FCSTD DOCUMENT  (FreeCAD 1.0R39109 (Git))
Label: 16_incher
License: All rights reserved
LicenseURL: http://en.wikipedia.org/wiki/All_rights_reserved
objects: Sketcher::SketchObject×32, Part::Feature×26, App::Part×21, Part::Extrusion×19, Part::FeaturePython×12, PartDesign::Pocket×7, Part::Mirroring×5, PartDesign::Body×4, PartDesign::PolarPattern×3, Part::Fillet×3, PartDesign::Pad×2, Part::Revolution×2, PartDesign::FeatureBase×2, PartDesign::Hole×2, Part::Sphere×1, Part::Cut×1
note: 171 computed .brp shape members not serialized (recipe doc carries the construction recipe); baked Part::Feature solids carry a one-line shape summary decoded from their .brp

FEATURE [Sketcher::SketchObject] Sketch003  label="mirror"
  ArcFitTolerance = 0
  FullyConstrained = false
  MakeInternals = false
  expr: Constraints[6] = 400 * 0.813985
  sketch-geometry (4):
    g0: Circle CenterX=0 CenterY=0 CenterZ=0 NormalX=0 NormalY=0 NormalZ=1 AngleXU=0 Radius=200
    g1: Circle [constr] CenterX=0 CenterY=0 CenterZ=0 NormalX=0 NormalY=0 NormalZ=1 AngleXU=0 Radius=112
    g2: Circle [constr] CenterX=0 CenterY=0 CenterZ=0 NormalX=0 NormalY=0 NormalZ=1 AngleXU=0 Radius=80.1102
    g3: Circle [constr] CenterX=0 CenterY=0 CenterZ=0 NormalX=0 NormalY=0 NormalZ=1 AngleXU=0 Radius=162.797
  constraints (7):
    c: Coincident(g0,g-1)
    c: Diameter(g0) = 400
    c: Coincident(g1,g0)
    c: Radius(g1) = 112
    c: Coincident(g2,g0)
    c: Coincident(g3,g0)
    c: Diameter(g3) = 325.594
FEATURE [Sketcher::SketchObject] Sketch006  label="alignment_ring"
  ArcFitTolerance = 0
  FullyConstrained = true
  MakeInternals = false
  Placement = pos=(0,0,-9) rot=(0,0,1;0rad)
  sketch-geometry (15):
    g0: Circle CenterX=-40 CenterY=69.282 CenterZ=0 NormalX=0 NormalY=0 NormalZ=1 AngleXU=0 Radius=3
    g1: Circle CenterX=0 CenterY=0 CenterZ=0 NormalX=0 NormalY=0 NormalZ=1 AngleXU=0 Radius=70
    g2: Circle CenterX=0 CenterY=0 CenterZ=0 NormalX=0 NormalY=0 NormalZ=1 AngleXU=0 Radius=90
    g3: LineSegment [constr] StartX=-40 StartY=69.282 StartZ=0 EndX=-80 EndY=-3.6e-15 EndZ=0
    g4: LineSegment [constr] StartX=-80 StartY=-3.6e-15 StartZ=0 EndX=-40 EndY=-69.282 EndZ=0
    g5: LineSegment [constr] StartX=-40 StartY=-69.282 StartZ=0 EndX=40 EndY=-69.282 EndZ=0
    g6: LineSegment [constr] StartX=40 StartY=-69.282 StartZ=0 EndX=80 EndY=-1.8e-15 EndZ=0
    g7: LineSegment [constr] StartX=80 StartY=-1.8e-15 StartZ=0 EndX=40 EndY=69.282 EndZ=0
    g8: LineSegment [constr] StartX=40 StartY=69.282 StartZ=0 EndX=-40 EndY=69.282 EndZ=0
    g9: Circle [constr] CenterX=0 CenterY=0 CenterZ=0 NormalX=0 NormalY=0 NormalZ=1 AngleXU=0 Radius=80
    g10: Circle CenterX=-80 CenterY=-3.6e-15 CenterZ=0 NormalX=0 NormalY=0 NormalZ=1 AngleXU=0 Radius=3
    g11: Circle CenterX=-40 CenterY=-69.282 CenterZ=0 NormalX=0 NormalY=0 NormalZ=1 AngleXU=0 Radius=3
    g12: Circle CenterX=40 CenterY=-69.282 CenterZ=0 NormalX=0 NormalY=0 NormalZ=1 AngleXU=0 Radius=3
    g13: Circle CenterX=80 CenterY=-1.8e-15 CenterZ=0 NormalX=0 NormalY=0 NormalZ=1 AngleXU=0 Radius=3
    g14: Circle CenterX=40 CenterY=69.282 CenterZ=0 NormalX=0 NormalY=0 NormalZ=1 AngleXU=0 Radius=3
  constraints (32):
    c: Diameter(g0) = 6
    c: Coincident(g2,g1)
    c: Diameter(g1) = 140
    c: Diameter(g2) = 180
    c: Coincident(g3,g4)
    c: Coincident(g4,g5)
    c: Coincident(g5,g6)
    c: Coincident(g6,g7)
    c: Coincident(g7,g8)
    c: Coincident(g8,g3)
    c: Equal(g3, g4-g8) x5
    c: PointOnObject(g3,g9)
    c: PointOnObject(g4,g9)
    c: PointOnObject(g5,g9)
    c: PointOnObject(g6,g9)
    c: PointOnObject(g7,g9)
    c: PointOnObject(g8,g9)
    c: Coincident(g9,g1)
    c: Diameter(g9) = 160
    c: Coincident(g1,g-1)
    c: Coincident(g0,g3)
    c: Diameter(g10) = 6
    c: Diameter(g11) = 6
    c: Diameter(g12) = 6
    c: Diameter(g13) = 6
    c: Diameter(g14) = 6
    c: Coincident(g13,g6)
    c: Coincident(g14,g7)
    c: Coincident(g12,g5)
    c: Coincident(g4,g11)
    c: Coincident(g10,g3)
    c: Parallel(g5,g-1)
FEATURE [Sketcher::SketchObject] Sketch008  label="linear_bearing"
  ArcFitTolerance = 0
  FullyConstrained = true
  MakeInternals = false
  sketch-geometry (1):
    g0: Circle CenterX=202.127 CenterY=113.881 CenterZ=0 NormalX=0 NormalY=0 NormalZ=1 AngleXU=0 Radius=10.5
  constraints (3):
    c: Diameter(g0) = 21
    c: DistanceX(g0) = 202.127
    c: DistanceY(g0) = 113.881
FEATURE [Sketcher::SketchObject] Sketch002  label="support_bar"
  ArcFitTolerance = 0
  FullyConstrained = true
  MakeInternals = false
  Placement = pos=(0,0,-15) rot=(0,0,1;0rad)
  sketch-geometry (17):
    g0: Circle CenterX=-65.7495 CenterY=113.882 CenterZ=0 NormalX=0 NormalY=0 NormalZ=1 AngleXU=0 Radius=2
    g1: Circle CenterX=65.7495 CenterY=113.882 CenterZ=0 NormalX=0 NormalY=0 NormalZ=1 AngleXU=0 Radius=2
    g2: LineSegment [constr] StartX=-65.7495 StartY=113.882 StartZ=0 EndX=65.7495 EndY=113.882 EndZ=0
    g3: Circle CenterX=0 CenterY=113.882 CenterZ=0 NormalX=0 NormalY=0 NormalZ=1 AngleXU=0 Radius=7
    g4: GeomPoint [constr] X=0 Y=113.882 Z=0
    g5: LineSegment StartX=-66.7324 StartY=119.801 StartZ=0 EndX=-16.3809 EndY=128.162 EndZ=0
    g6: LineSegment StartX=66.7324 StartY=119.801 StartZ=0 EndX=16.3809 EndY=128.162 EndZ=0
    g7: Circle [constr] CenterX=-65.7495 CenterY=113.882 CenterZ=0 NormalX=0 NormalY=0 NormalZ=1 AngleXU=0 Radius=6
    g8: LineSegment StartX=-16.3809 StartY=99.6021 StartZ=0 EndX=-66.7324 EndY=107.963 EndZ=0
    g9: LineSegment StartX=16.3809 StartY=99.6021 StartZ=0 EndX=66.7324 EndY=107.963 EndZ=0
    g10: ArcOfCircle CenterX=-65.7495 CenterY=113.882 CenterZ=0 NormalX=0 NormalY=0 NormalZ=1 AngleXU=0 Radius=6 StartAngle=1.73535 EndAngle=4.54784
    g11: ArcOfCircle CenterX=65.7495 CenterY=113.882 CenterZ=0 NormalX=0 NormalY=0 NormalZ=1 AngleXU=0 Radius=6 StartAngle=4.87694 EndAngle=7.68943
    g12: Circle [constr] CenterX=65.7495 CenterY=113.882 CenterZ=0 NormalX=0 NormalY=0 NormalZ=1 AngleXU=0 Radius=6
    g13: ArcOfCircle CenterX=5.9e-15 CenterY=29.5127 CenterZ=0 NormalX=0 NormalY=0 NormalZ=1 AngleXU=0 Radius=100 StartAngle=1.40625 EndAngle=1.73535
    g14: GeomPoint [constr] X=0 Y=130.882 Z=0
    g15: ArcOfCircle CenterX=-5.8e-15 CenterY=198.251 CenterZ=0 NormalX=0 NormalY=0 NormalZ=1 AngleXU=0 Radius=100 StartAngle=4.54784 EndAngle=4.87694
    g16: GeomPoint [constr] X=0 Y=96.882 Z=0
  constraints (38):
    c: Equal(g0,g1)
    c: Distance(g0,g1) = 131.499
    c: Coincident(g2,g0)
    c: Coincident(g2,g1)
    c: Symmetric(g0,g1,g3)
    c: Diameter(g3) = 14
    c: Diameter(g0) = 4
    c: Coincident(g4,g3)
    c: Parallel(g2,g-1)
    c: Coincident(g7,g0)
    c: Diameter(g7) = 12
    c: PointOnObject(g3,g-2)
    c: DistanceY(g-1,g3) = 113.882
    c: PointOnObject(g14,g-2)
    c: Symmetric(g16,g14,g2)
    c: Tangent(g8,g7)
    c: Distance(g14,g16) = 34
    c: Tangent(g5,g10) = 1.5708
    c: Tangent(g8,g10) = 1.5708
    c: Equal(g7,g10)
    c: Tangent(g6,g11) = -1.5708
    c: Tangent(g9,g11) = -1.5708
    c: Coincident(g12,g1)
    c: Tangent(g12,g9)
    c: Equal(g12,g7)
    c: Tangent(g6,g12)
    c: Equal(g11,g7)
    c: Tangent(g5,g7)
    c: PointOnObject(g14,g5)
    c: PointOnObject(g14,g6)
    c: Tangent(g5,g13) = 1.5708
    c: Tangent(g6,g13) = -1.5708
    c: PointOnObject(g16,g8)
    c: PointOnObject(g16,g9)
    c: Tangent(g8,g15) = 1.5708
    c: Tangent(g9,g15) = -1.5708
    c: Equal(g15,g13)
    c: Diameter(g13) = 200
FEATURE [Sketcher::SketchObject] Sketch001  label="support_triangle"
  ArcFitTolerance = 0
  FullyConstrained = true
  MakeInternals = false
  Placement = pos=(0,0,-5) rot=(0,0,1;0rad)
  sketch-geometry (19):
    g0: LineSegment [constr] StartX=157.248 StartY=42.135 StartZ=0 EndX=80.0037 EndY=1.25412e-06 EndZ=0
    g1: LineSegment [constr] StartX=80.0037 StartY=1.25412e-06 StartZ=0 EndX=157.248 EndY=-42.135 EndZ=0
    g2: LineSegment [constr] StartX=157.248 StartY=-42.135 StartZ=0 EndX=157.248 EndY=42.135 EndZ=0
    g3: Circle CenterX=157.248 CenterY=42.135 CenterZ=0 NormalX=0 NormalY=0 NormalZ=1 AngleXU=0 Radius=3
    g4: Circle CenterX=80.0037 CenterY=1.25412e-06 CenterZ=0 NormalX=0 NormalY=0 NormalZ=1 AngleXU=0 Radius=3
    g5: Circle CenterX=157.248 CenterY=-42.135 CenterZ=0 NormalX=0 NormalY=0 NormalZ=1 AngleXU=0 Radius=3
    g6: LineSegment [constr] StartX=118.626 StartY=-21.0675 StartZ=0 EndX=157.248 EndY=42.135 EndZ=0
    g7: LineSegment [constr] StartX=80.0037 StartY=1.25412e-06 StartZ=0 EndX=157.248 EndY=2.46499e-06 EndZ=0
    g8: Circle CenterX=131.5 CenterY=2.06137e-06 CenterZ=0 NormalX=0 NormalY=0 NormalZ=1 AngleXU=0 Radius=6
    g9: LineSegment [constr] StartX=157.248 StartY=-42.135 StartZ=0 EndX=118.626 EndY=21.0675 EndZ=0
    g10: LineSegment StartX=154.255 StartY=47.6218 StartZ=0 EndX=77.0108 EndY=5.4868 EndZ=0
    g11: LineSegment StartX=77.0108 StartY=-5.4868 StartZ=0 EndX=154.255 EndY=-47.6218 EndZ=0
    g12: LineSegment StartX=163.498 StartY=-42.135 StartZ=0 EndX=163.498 EndY=42.135 EndZ=0
    g13: Circle [constr] CenterX=80.0037 CenterY=1.25412e-06 CenterZ=0 NormalX=0 NormalY=0 NormalZ=1 AngleXU=0 Radius=6.25
    g14: Circle [constr] CenterX=157.248 CenterY=42.135 CenterZ=0 NormalX=0 NormalY=0 NormalZ=1 AngleXU=0 Radius=6.25
    g15: Circle [constr] CenterX=157.248 CenterY=-42.135 CenterZ=0 NormalX=0 NormalY=0 NormalZ=1 AngleXU=0 Radius=6.25
    g16: ArcOfCircle CenterX=80.0037 CenterY=1.25412e-06 CenterZ=0 NormalX=0 NormalY=0 NormalZ=1 AngleXU=0 Radius=6.25 StartAngle=2.07016 EndAngle=4.21303
    g17: ArcOfCircle CenterX=157.248 CenterY=-42.135 CenterZ=0 NormalX=0 NormalY=0 NormalZ=1 AngleXU=0 Radius=6.25 StartAngle=4.21303 EndAngle=6.28319
    g18: ArcOfCircle CenterX=157.248 CenterY=42.135 CenterZ=0 NormalX=0 NormalY=0 NormalZ=1 AngleXU=0 Radius=6.25 StartAngle=1.56758e-08 EndAngle=2.07016
  constraints (45):
    c: Coincident(g0,g1)
    c: Coincident(g1,g2)
    c: Coincident(g2,g0)
    c: Distance(g1) = 87.989
    c: Coincident(g4,g0)
    c: Coincident(g5,g1)
    c: Equal(g4,g5)
    c: Equal(g4,g3)
    c: Coincident(g6,g3)
    c: Coincident(g7,g4)
    c: Symmetric(g4,g5,g6)
    c: Symmetric(g5,g3,g7)
    c: PointOnObject(g8,g6)
    c: PointOnObject(g8,g7)
    c: Coincident(g9,g5)
    c: Symmetric(g3,g4,g9)
    c: Diameter(g3) = 6
    c: Diameter(g8) = 12
    c: Distance(g2) = 84.27
    c: Coincident(g3,g0)
    c: Equal(g0,g1)
    c: Parallel(g10,g0)
    c: Parallel(g11,g1)
    c: Parallel(g12,g2)
    c: Coincident(g13,g4)
    c: Coincident(g14,g3)
    c: Coincident(g15,g5)
    c: Equal(g15,g13)
    c: Equal(g13,g14)
    c: Diameter(g14) = 12.5
    c: Tangent(g11,g13)
    c: Tangent(g10,g13)
    c: Tangent(g12,g15)
    c: Distance(g-1,g8) = 131.5
    c: PointOnObject(g-1,g7)
    c: Tangent(g11,g16) = -1.5708
    c: Tangent(g10,g16) = -1.5708
    c: Diameter(g16) = 12.5
    c: Tangent(g11,g17) = -1.5708
    c: Tangent(g12,g17) = -1.5708
    c: Equal(g17,g16)
    c: Tangent(g10,g18) = -1.5708
    c: Tangent(g12,g18) = -1.5708
    c: Equal(g18,g16)
    c: DistanceX(g-2,g8) = 131.5
FEATURE [Part::Extrusion] Extrude  label="triangle_extrude"
  Base = -> Sketch001
  Dir = (0,0,1)
  DirMode = 2
  FaceMakerClass = Part::FaceMakerBullseye
  FaceMakerMode = 3
  LengthFwd = -3
  LengthRev = 0
  Placement = pos=(0,0,0) rot=(0,0,1;1.0472rad)
  Solid = true
  Symmetric = false
FEATURE [Sketcher::SketchObject] Sketch  label="mirror_cell"
  ArcFitTolerance = 0
  FullyConstrained = true
  MakeInternals = false
  expr: Constraints[22] = 400 * 0.400016
  expr: Constraints[23] = 400 * 0.813953
  expr: Constraints[35] = 113.882 * 2
  sketch-geometry (17):
    g0: Circle [constr] CenterX=0 CenterY=0 CenterZ=0 NormalX=0 NormalY=0 NormalZ=1 AngleXU=0 Radius=162.791
    g1: LineSegment StartX=-225 StartY=123.882 StartZ=0 EndX=225 EndY=123.882 EndZ=0
    g2: LineSegment StartX=225 StartY=123.882 StartZ=0 EndX=225 EndY=103.882 EndZ=0
    g3: LineSegment StartX=225 StartY=103.882 StartZ=0 EndX=-225 EndY=103.882 EndZ=0
    g4: LineSegment StartX=-225 StartY=103.882 StartZ=0 EndX=-225 EndY=123.882 EndZ=0
    g5: Circle CenterX=-98.6247 CenterY=113.882 CenterZ=0 NormalX=0 NormalY=0 NormalZ=1 AngleXU=0 Radius=2.9
    g6: Circle CenterX=98.6247 CenterY=113.882 CenterZ=0 NormalX=0 NormalY=0 NormalZ=1 AngleXU=0 Radius=2.9
    g7: Circle CenterX=-202 CenterY=113.882 CenterZ=0 NormalX=0 NormalY=0 NormalZ=1 AngleXU=0 Radius=2.9
    g8: Circle CenterX=202 CenterY=113.882 CenterZ=0 NormalX=0 NormalY=0 NormalZ=1 AngleXU=0 Radius=2.9
    g9: LineSegment [constr] StartX=-202 StartY=113.882 StartZ=0 EndX=202 EndY=113.882 EndZ=0
    g10: Circle [constr] CenterX=0 CenterY=0 CenterZ=0 NormalX=0 NormalY=0 NormalZ=1 AngleXU=0 Radius=80.0032
    g11: Circle CenterX=1.2e-15 CenterY=113.882 CenterZ=0 NormalX=0 NormalY=0 NormalZ=1 AngleXU=0 Radius=2.9
    g12: LineSegment [constr] StartX=1.2e-15 StartY=113.882 StartZ=0 EndX=-98.6247 EndY=-56.941 EndZ=0
    g13: LineSegment [constr] StartX=-98.6247 StartY=-56.941 StartZ=0 EndX=98.6247 EndY=-56.941 EndZ=0
    g14: LineSegment [constr] StartX=98.6247 StartY=-56.941 StartZ=0 EndX=1.2e-15 EndY=113.882 EndZ=0
    g15: Circle [constr] CenterX=0 CenterY=0 CenterZ=0 NormalX=0 NormalY=0 NormalZ=1 AngleXU=0 Radius=113.882
    g16: LineSegment [constr] StartX=-98.6247 StartY=-56.941 StartZ=0 EndX=-98.6247 EndY=113.882 EndZ=0
  constraints (41):
    c: Coincident(g1,g2)
    c: Coincident(g2,g3)
    c: Coincident(g3,g4)
    c: Coincident(g4,g1)
    c: Horizontal(g1)
    c: Vertical(g2)
    c: Symmetric(g3,g2,g-2)
    c: Distance(g4) = 20
    c: Symmetric(g7,g8,g-2)
    c: Equal(g7,g5)
    c: Equal(g7,g6)
    c: Equal(g7,g8)
    c: Diameter(g7) = 5.8
    c: Coincident(g9,g7)
    c: Coincident(g9,g8)
    c: Distance(g9) = 404
    c: Distance(g1) = 450
    c: Symmetric(g1,g3,g9)
    c: PointOnObject(g11,g-2)
    c: PointOnObject(g11,g9)
    c: Equal(g11,g5)
    c: Symmetric(g6,g5,g-2)
    c: Diameter(g10) = 160.006
    c: Diameter(g0) = 325.581
    c: PointOnObject(g5,g9)
    c: Coincident(g12,g13)
    c: Coincident(g13,g14)
    c: Coincident(g14,g12)
    c: Equal(g12,g13)
    c: Equal(g12,g14)
    c: PointOnObject(g12,g15)
    c: PointOnObject(g13,g15)
    c: PointOnObject(g14,g15)
    c: Coincident(g15,g0)
    c: Coincident(g14,g11)
    c: Diameter(g15) = 227.764
    c: Coincident(g0,g10)
    c: Coincident(g0,g-1)
    c: Coincident(g16,g12)
    c: Coincident(g16,g5)
    c: Parallel(g16,g-2)
FEATURE [Sketcher::SketchObject] Sketch007  label="bearing_shaft"
  ArcFitTolerance = 0
  ExternalGeometry = -> [Sketch]
  FullyConstrained = true
  MakeInternals = false
  Placement = pos=(0,0,-20) rot=(0,0,1;0rad)
  sketch-geometry (1):
    g0: Circle CenterX=-202 CenterY=113.882 CenterZ=0 NormalX=0 NormalY=0 NormalZ=1 AngleXU=0 Radius=6
  constraints (2):
    c: Diameter(g0) = 12
    c: Coincident(g0,g-3)
FEATURE [Part::Extrusion] Extrude001  label="support_bar_extrude"
  Base = -> Sketch002
  Dir = (0,0,1)
  DirMode = 2
  FaceMakerClass = Part::FaceMakerBullseye
  FaceMakerMode = 3
  LengthFwd = 6
  LengthRev = 0
  Solid = true
  Symmetric = false
FEATURE [Part::Extrusion] Extrude002  label="mirror_extrude"
  Base = -> Sketch003
  Dir = (0,0,1)
  DirMode = 2
  FaceMakerClass = Part::FaceMakerBullseye
  FaceMakerMode = 3
  LengthFwd = 25
  LengthRev = 0
  Solid = true
  Symmetric = false
FEATURE [Part::Extrusion] Extrude003  label="cell_bar"
  Base = -> Sketch
  Dir = (0,0,1)
  DirMode = 2
  FaceMakerClass = Part::FaceMakerBullseye
  FaceMakerMode = 3
  LengthFwd = 20
  LengthRev = 0
  Placement = pos=(0,0,-37) rot=(0,0,1;0rad)
  Solid = true
  Symmetric = false
FEATURE [Part::Extrusion] Extrude004  label="bearing_shaft_extrude"
  Base = -> Sketch007
  Dir = (0,0,1)
  DirMode = 2
  FaceMakerClass = Part::FaceMakerBullseye
  FaceMakerMode = 3
  LengthFwd = 100
  LengthRev = 0
  Solid = true
  Symmetric = false
FEATURE [Part::Mirroring] Part__Mirroring  label="bearing_shaft_extrude (Mirror #1)"
  Base = (0,0,0)
  Normal = (1,0,0)
  Source = -> Extrude004
FEATURE [Part::Extrusion] Extrude005  label="linear_bearing_extrude"
  Base = -> Sketch008
  Dir = (0,0,1)
  DirMode = 2
  FaceMakerClass = Part::FaceMakerBullseye
  FaceMakerMode = 3
  LengthFwd = 30
  LengthRev = 0
  Solid = true
  Symmetric = false
FEATURE [Part::Mirroring] Part__Mirroring001  label="linear_bearing_extrude (Mirror #2)"
  Base = (0,0,0)
  Normal = (1,0,0)
  Source = -> Extrude005
FEATURE [Part::Extrusion] Extrude006  label="alignment_ring_extrude"
  Base = -> Sketch006
  Dir = (0,0,1)
  DirMode = 2
  FaceMakerClass = Part::FaceMakerBullseye
  FaceMakerMode = 3
  LengthFwd = 1
  LengthRev = 0
  Solid = true
  Symmetric = false
FEATURE [Sketcher::SketchObject] Sketch009  label="altitude_bearing"
  ArcFitTolerance = 0
  FullyConstrained = false
  MakeInternals = false
  Placement = pos=(225,0,0) rot=(0.57735,0.57735,0.57735;2.0944rad)
  sketch-geometry (6):
    g0: ArcOfCircle CenterX=0 CenterY=338.702 CenterZ=0 NormalX=0 NormalY=0 NormalZ=1 AngleXU=0 Radius=400 StartAngle=3.11112 EndAngle=5.38005
    g1: ArcOfCircle CenterX=0 CenterY=338.702 CenterZ=0 NormalX=0 NormalY=0 NormalZ=1 AngleXU=0 Radius=325 StartAngle=3.11112 EndAngle=5.38005
    g2: LineSegment [constr] StartX=0 StartY=338.702 StartZ=0 EndX=-399.814 EndY=350.888 EndZ=0
    g3: LineSegment [constr] StartX=0 StartY=338.702 StartZ=0 EndX=247.661 EndY=24.5937 EndZ=0
    g4: LineSegment StartX=-399.814 StartY=350.888 StartZ=0 EndX=-324.849 EndY=348.604 EndZ=0
    g5: LineSegment StartX=247.661 StartY=24.5937 StartZ=0 EndX=201.224 EndY=83.4891 EndZ=0
  constraints (16):
    c: Coincident(g1,g0)
    c: Diameter(g1) = 650
    c: Diameter(g0) = 800
    c: Coincident(g2,g0)
    c: Coincident(g2,g0)
    c: Coincident(g3,g0)
    c: Coincident(g3,g0)
    c: PointOnObject(g1,g2)
    c: PointOnObject(g1,g3)
    c: Angle(g2,g3) = 2.26893
    c: Coincident(g4,g0)
    c: Coincident(g4,g1)
    c: Coincident(g5,g0)
    c: Coincident(g5,g1)
    c: PointOnObject(g0,g-2)
    c: DistanceY(g0) = 338.702
FEATURE [Part::Extrusion] Extrude007  label="altitude_bearing_extrude"
  Base = -> Sketch009
  Dir = (1,0,0)
  DirMode = 2
  FaceMakerClass = Part::FaceMakerBullseye
  FaceMakerMode = 3
  LengthFwd = 20
  LengthRev = 0
  Solid = true
  Symmetric = false
FEATURE [Part::Mirroring] Part__Mirroring002  label="altitude_bearing_extrude (Mirror #3)"
  Base = (0,0,0)
  Normal = (1,0,0)
  Source = -> Extrude007
FEATURE [Sketcher::SketchObject] Sketch010  label="uta_ring"
  ArcFitTolerance = 0
  AttachmentSupport = -> [XY_Plane]
  FullyConstrained = true
  MakeInternals = false
  MapMode = 5
  expr: Constraints[3] = Constraints[1] + 60 mm
  sketch-geometry (3):
    g0: Circle CenterX=0 CenterY=0 CenterZ=0 NormalX=0 NormalY=0 NormalZ=1 AngleXU=0 Radius=225
    g1: ArcOfCircle CenterX=0 CenterY=0 CenterZ=0 NormalX=0 NormalY=0 NormalZ=1 AngleXU=0 Radius=255 StartAngle=2.12261 EndAngle=8.03521
    g2: LineSegment StartX=-133.679 StartY=217.152 StartZ=0 EndX=-45.9599 EndY=250.824 EndZ=0
  constraints (8):
    c: Coincident(g0,g-1)
    c: Diameter(g0) = 450
    c: Coincident(g1,g0)
    c: Diameter(g1) = 510
    c: Distance(g2) = 93.96
    c: Coincident(g1,g2)
    c: Coincident(g1,g2)
    c: Angle(g-1,g2) = 0.366519
FEATURE [PartDesign::Pad] Pad  label="uta_ring_pad"
  Direction = (0,0,1)
  Length = 4.8
  Length2 = 10
  Profile = -> Sketch010
  ReferenceAxis = -> Sketch010 [N_Axis]
  Suppressed = false
  Type = 0
FEATURE [Sketcher::SketchObject] Sketch011  label="mounting_hole"
  ArcFitTolerance = 0
  AttachmentSupport = -> [Pad]
  FullyConstrained = true
  MakeInternals = false
  MapMode = 5
  Placement = pos=(0,0,4.8) rot=(0,0,1;0rad)
  expr: Constraints[0] = (<<uta_ring>>.Constraints[1] + <<uta_ring>>.Constraints[3]) / 2
  sketch-geometry (3):
    g0: Circle [constr] CenterX=0 CenterY=0 CenterZ=0 NormalX=0 NormalY=0 NormalZ=1 AngleXU=0 Radius=240
    g1: Circle CenterX=0 CenterY=240 CenterZ=0 NormalX=0 NormalY=0 NormalZ=1 AngleXU=0 Radius=3
    g2: Circle [constr] CenterX=0 CenterY=240 CenterZ=0 NormalX=0 NormalY=0 NormalZ=1 AngleXU=0 Radius=5
  constraints (7):
    c: Diameter(g0) = 480
    c: Diameter(g1) = 6
    c: PointOnObject(g1,g-2)
    c: Coincident(g0,g-1)
    c: PointOnObject(g1,g0)
    c: Coincident(g2,g1)
    c: Diameter(g2) = 10
FEATURE [PartDesign::Pocket] Pocket  label="mounting_hole_pocket"
  BaseFeature = -> Pad
  Direction = (0,0,-1)
  Length = 5
  Length2 = 5
  Profile = -> Sketch011
  ReferenceAxis = -> Sketch011 [N_Axis]
  Suppressed = false
  Type = 1
FEATURE [Sketcher::SketchObject] Sketch012  label="weight_saving_hole"
  ArcFitTolerance = 0
  AttachmentOffset = pos=(0,0,0) rot=(0,0,1;1.0472rad)
  AttachmentSupport = -> [Pocket]
  FullyConstrained = false
  MakeInternals = false
  MapMode = 5
  Placement = pos=(0,0,4.8) rot=(0,0,1;1.0472rad)
  expr: Constraints[12] = Constraints[4]
  expr: Constraints[16] = Constraints[4]
  expr: Constraints[1] = (<<uta_ring>>.Constraints[1] + <<uta_ring>>.Constraints[3]) / 2
  expr: Constraints[6] = Constraints[4]
  expr: Constraints[9] = Constraints[7] * 2
  sketch-geometry (10):
    g0: Circle [constr] CenterX=9.8e-15 CenterY=-3.2e-14 CenterZ=0 NormalX=0 NormalY=0 NormalZ=1 AngleXU=0 Radius=240
    g1: LineSegment [constr] StartX=-37.5443 StartY=237.045 StartZ=0 EndX=9.8e-15 EndY=-3.52e-14 EndZ=0
    g2: LineSegment [constr] StartX=-62.1166 StartY=231.822 StartZ=0 EndX=-4.4e-15 EndY=7.1e-15 EndZ=0
    g3: LineSegment [constr] StartX=-86.0083 StartY=224.059 StartZ=0 EndX=1.82e-14 EndY=-1.59e-14 EndZ=0
    g4: LineSegment [constr] StartX=-151.037 StartY=186.515 StartZ=0 EndX=-3.4e-15 EndY=-3.45e-14 EndZ=0
    g5: LineSegment [constr] StartX=-169.706 StartY=169.706 StartZ=0 EndX=7.1e-15 EndY=-3.2e-14 EndZ=0
    g6: LineSegment [constr] StartX=9.8e-15 StartY=-3.2e-14 StartZ=0 EndX=-186.515 EndY=151.037 EndZ=0
    g7: Circle CenterX=-86.0083 CenterY=224.059 CenterZ=0 NormalX=0 NormalY=0 NormalZ=1 AngleXU=0 Radius=7.5
    g8: Circle CenterX=-62.1166 CenterY=231.822 CenterZ=0 NormalX=0 NormalY=0 NormalZ=1 AngleXU=0 Radius=7.5
    g9: Circle CenterX=-37.5443 CenterY=237.045 CenterZ=0 NormalX=0 NormalY=0 NormalZ=1 AngleXU=0 Radius=7.5
  constraints (25):
    c: Coincident(g0,g-1)
    c: Diameter(g0) = 480
    c: Coincident(g1,g0)
    c: Coincident(g2,g0)
    c: Angle(g1,g2) = 0.10472
    c: Coincident(g3,g0)
    c: Angle(g2,g3) = 0.10472
    c: Angle(g-2,g1) = 0.15708
    c: Coincident(g4,g0)
    c: Angle(g3,g4) = 0.314159
    c: PointOnObject(g5,g0)
    c: Coincident(g5,g0)
    c: Angle(g4,g5) = 0.10472
    c: PointOnObject(g1,g0)
    c: Coincident(g6,g0)
    c: PointOnObject(g6,g0)
    c: Angle(g5,g6) = 0.10472
    c: Coincident(g7,g3)
    c: Coincident(g8,g2)
    c: Coincident(g9,g1)
    c: Equal(g9,g8)
    c: Equal(g8,g7)
    c: PointOnObject(g8,g0)
    c: PointOnObject(g7,g0)
    c: Diameter(g9) = 15
FEATURE [PartDesign::Pocket] Pocket001  label="weight_saving_hole_pocket"
  BaseFeature = -> Pocket
  Direction = (0,0,-1)
  Length = 5
  Length2 = 5
  Profile = -> Sketch012
  ReferenceAxis = -> Sketch012 [N_Axis]
  Suppressed = false
  Type = 1
FEATURE [Sketcher::SketchObject] Sketch013  label="alignment_hole"
  ArcFitTolerance = 0
  AttachmentSupport = -> [Pocket001]
  FullyConstrained = false
  MakeInternals = false
  MapMode = 5
  Placement = pos=(0,0,4.8) rot=(0,0,1;0rad)
  expr: Constraints[1] = ((<<uta_ring>>.Constraints[1] + <<uta_ring>>.Constraints[3]) / 2 + 20 mm) / 2
  expr: Constraints[2] = Sketch023.Constraints[29]
  sketch-geometry (5):
    g0: LineSegment [constr] StartX=-1.00956 StartY=0.394562 StartZ=0 EndX=-229.037 EndY=102.881 EndZ=0
    g1: Circle CenterX=-229.037 CenterY=102.881 CenterZ=0 NormalX=0 NormalY=0 NormalZ=1 AngleXU=0 Radius=1.5
    g2: Circle CenterX=-208.599 CenterY=93.9422 CenterZ=0 NormalX=0 NormalY=0 NormalZ=1 AngleXU=0 Radius=1.5
    g3: Circle CenterX=-185.613 CenterY=133.6 CenterZ=0 NormalX=0 NormalY=0 NormalZ=1 AngleXU=0 Radius=1.5
    g4: Circle CenterX=-203.674 CenterY=146.861 CenterZ=0 NormalX=0 NormalY=0 NormalZ=1 AngleXU=0 Radius=1.5
  constraints (6):
    c: Coincident(g1,g0)
    c: Distance(g0) = 250
    c: Diameter(g1) = 3
    c: Equal(g2,g1)
    c: Equal(g1,g3)
    c: Equal(g3,g4)
FEATURE [Sketcher::SketchObject] Sketch014  label="focuser_mounting_holes"
  ArcFitTolerance = 0
  AttachmentSupport = -> [Pad]
  ExternalGeometry = -> [Sketch010]
  FullyConstrained = false
  MakeInternals = false
  MapMode = 5
  Placement = pos=(0,0,4.8) rot=(0,0,1;0rad)
  expr: Constraints[8] = (<<uta_ring>>.Constraints[1] + <<uta_ring>>.Constraints[3]) / 4
  sketch-geometry (4):
    g0: Circle CenterX=-119.961 CenterY=207.869 CenterZ=0 NormalX=0 NormalY=0 NormalZ=1 AngleXU=0 Radius=3
    g1: Circle CenterX=-49.9426 CenterY=234.746 CenterZ=0 NormalX=0 NormalY=0 NormalZ=1 AngleXU=0 Radius=3
    g2: LineSegment [constr] StartX=-89.8195 StartY=233.988 StartZ=0 EndX=-93.4226 EndY=243.374 EndZ=0
    g3: LineSegment [constr] StartX=-119.961 StartY=207.869 StartZ=0 EndX=-49.9426 EndY=234.746 EndZ=0
  constraints (9):
    c: Equal(g0,g1)
    c: Diameter(g0) = 6
    c: PointOnObject(g2,g-3)
    c: Symmetric(g-3,g-3,g2)
    c: Symmetric(g0,g1,g2)
    c: Coincident(g3,g0)
    c: Coincident(g3,g1)
    c: Distance(g3) = 75
    c: Distance(g-1,g0) = 240
FEATURE [Sketcher::SketchObject] Sketch016  label="focuser_plate"
  ArcFitTolerance = 0
  AttachmentSupport = -> [XZ_Plane007]
  FullyConstrained = true
  MakeInternals = false
  MapMode = 5
  Placement = pos=(0,0,0) rot=(1,0,0;1.5708rad)
  expr: Constraints[11] = 2.715 * 25.4
  expr: Constraints[17] = 0.166 * 25.4
  expr: Constraints[1] = 2.375 * 25.4
  expr: Constraints[27] = Constraints[11] + 25 mm
  sketch-geometry (13):
    g0: Circle CenterX=0 CenterY=0 CenterZ=0 NormalX=0 NormalY=0 NormalZ=1 AngleXU=0 Radius=30.1625
    g1: LineSegment [constr] StartX=29.861 StartY=-17.2403 StartZ=0 EndX=-7e-16 EndY=34.4805 EndZ=0
    g2: LineSegment [constr] StartX=-7e-16 StartY=34.4805 StartZ=0 EndX=-29.861 EndY=-17.2403 EndZ=0
    g3: LineSegment [constr] StartX=-29.861 StartY=-17.2403 StartZ=0 EndX=29.861 EndY=-17.2403 EndZ=0
    g4: Circle [constr] CenterX=0 CenterY=0 CenterZ=0 NormalX=0 NormalY=0 NormalZ=1 AngleXU=0 Radius=34.4805
    g5: Circle CenterX=-29.861 CenterY=-17.2403 CenterZ=0 NormalX=0 NormalY=0 NormalZ=1 AngleXU=0 Radius=2.1082
    g6: Circle CenterX=-7e-16 CenterY=34.4805 CenterZ=0 NormalX=0 NormalY=0 NormalZ=1 AngleXU=0 Radius=2.1082
    g7: Circle CenterX=29.861 CenterY=-17.2403 CenterZ=0 NormalX=0 NormalY=0 NormalZ=1 AngleXU=0 Radius=2.1082
    g8: ArcOfCircle CenterX=0 CenterY=0 CenterZ=0 NormalX=0 NormalY=0 NormalZ=1 AngleXU=0 Radius=46.9805 StartAngle=1e-16 EndAngle=3.14159
    g9: LineSegment StartX=-46.9805 StartY=5.8e-15 StartZ=0 EndX=-46.9805 EndY=-40 EndZ=0
    g10: LineSegment StartX=46.9805 StartY=4.7e-15 StartZ=0 EndX=46.9805 EndY=-40 EndZ=0
    g11: LineSegment StartX=-46.9805 StartY=-40 StartZ=0 EndX=46.9805 EndY=-40 EndZ=0
    g12: Circle [constr] CenterX=0 CenterY=0 CenterZ=0 NormalX=0 NormalY=0 NormalZ=1 AngleXU=0 Radius=37.5
  constraints (31):
    c: Coincident(g0,g-1)
    c: Diameter(g0) = 60.325
    c: Coincident(g1,g2)
    c: Coincident(g2,g3)
    c: Coincident(g3,g1)
    c: Equal(g1,g2)
    c: Equal(g1,g3)
    c: PointOnObject(g1,g4)
    c: PointOnObject(g2,g4)
    c: PointOnObject(g3,g4)
    c: Coincident(g4,g0)
    c: Diameter(g4) = 68.961
    c: Coincident(g5,g2)
    c: Coincident(g6,g1)
    c: Coincident(g7,g1)
    c: Equal(g7,g5)
    c: Equal(g5,g6)
    c: Diameter(g7) = 4.2164
    c: Coincident(g8,g0)
    c: Equal(g9,g10)
    c: Coincident(g11,g9)
    c: Coincident(g11,g10)
    c: Horizontal(g11)
    c: Parallel(g9,g10)
    c: Tangent(g8,g9) = -1.5708
    c: Tangent(g8,g10) = 1.5708
    c: Perpendicular(g-2,g3)
    c: Diameter(g8) = 93.961
    c: Distance(g9) = 40
    c: Coincident(g12,g0)
    c: Diameter(g12) = 75
FEATURE [PartDesign::Pad] Pad005
  Direction = (0,-1,2e-16)
  Length = 14
  Length2 = 10
  Placement = pos=(0,0,0) rot=(1,0,0;1.5708rad)
  Profile = -> Sketch016
  ReferenceAxis = -> Sketch016 [N_Axis]
  Suppressed = false
  Type = 0
FEATURE [Sketcher::SketchObject] Sketch017
  ArcFitTolerance = 0
  AttachmentSupport = -> [Pad005]
  ExternalGeometry = -> [Pad005]
  FullyConstrained = true
  MakeInternals = false
  MapMode = 5
  Placement = pos=(0,-8.9e-15,-40) rot=(1,0,0;3.14159rad)
  sketch-geometry (3):
    g0: Circle CenterX=-37.5 CenterY=7 CenterZ=0 NormalX=0 NormalY=0 NormalZ=1 AngleXU=0 Radius=3
    g1: Circle CenterX=37.5 CenterY=7 CenterZ=0 NormalX=0 NormalY=0 NormalZ=1 AngleXU=0 Radius=3
    g2: LineSegment [constr] StartX=-37.5 StartY=7 StartZ=0 EndX=37.5 EndY=7 EndZ=0
  constraints (7):
    c: Equal(g0,g1)
    c: Diameter(g0) = 6
    c: Coincident(g2,g0)
    c: Coincident(g2,g1)
    c: Symmetric(g1,g0,g-2)
    c: Distance(g0,g-3) = 7
    c: Distance(g2) = 75
FEATURE [PartDesign::Pocket] Pocket005
  BaseFeature = -> Pad005
  Direction = (0,0,1)
  Length = 5
  Length2 = 5
  Placement = pos=(0,0,0) rot=(1,0,0;1.5708rad)
  Profile = -> Sketch017
  ReferenceAxis = -> Sketch017 [N_Axis]
  Suppressed = false
  Type = 1
FEATURE [Sketcher::SketchObject] Sketch018
  ArcFitTolerance = 0
  AttachmentOffset = pos=(0,0,-59) rot=(0,0,1;0rad)
  AttachmentSupport = -> [Pocket005]
  ExternalGeometry = -> [Pocket005]
  FullyConstrained = true
  MakeInternals = false
  MapMode = 5
  Placement = pos=(0,-8.9e-15,19) rot=(1,0,0;3.14159rad)
  sketch-geometry (2):
    g0: Circle CenterX=-37.5 CenterY=7 CenterZ=0 NormalX=0 NormalY=0 NormalZ=1 AngleXU=0 Radius=5.5
    g1: Circle CenterX=37.5 CenterY=7 CenterZ=0 NormalX=0 NormalY=0 NormalZ=1 AngleXU=0 Radius=5.5
  constraints (4):
    c: Coincident(g0,g-3)
    c: Coincident(g1,g-4)
    c: Equal(g0,g1)
    c: Diameter(g1) = 11
FEATURE [PartDesign::Pocket] Pocket006
  BaseFeature = -> Pocket005
  Direction = (0,0,1)
  Length = 16
  Length2 = 5
  Placement = pos=(0,0,0) rot=(1,0,0;1.5708rad)
  Profile = -> Sketch018
  ReferenceAxis = -> Sketch018 [N_Axis]
  Suppressed = false
  Type = 0
FEATURE [PartDesign::Body] Body007  label="focuser_plate_body"
  AllowCompound = false
  Group = -> [Sketch016,Pad005,Sketch017,Pocket005,Sketch018,Pocket006]
  Origin = -> Origin007
  Tip = -> Pocket006
FEATURE [Sketcher::SketchObject] Sketch025  label="truss_pole"
  ArcFitTolerance = 0
  FullyConstrained = true
  MakeInternals = false
  sketch-geometry (3):
    g0: Circle CenterX=-268.468 CenterY=155 CenterZ=0 NormalX=0 NormalY=0 NormalZ=1 AngleXU=0 Radius=12.5
    g1: LineSegment [constr] StartX=-268.468 StartY=155 StartZ=0 EndX=-1.096e-13 EndY=1.137e-13 EndZ=0
    g2: Circle CenterX=-268.468 CenterY=155 CenterZ=0 NormalX=0 NormalY=0 NormalZ=1 AngleXU=0 Radius=11.5
  constraints (7):
    c: Diameter(g0) = 25
    c: Distance(g-1,g0) = 310
    c: Coincident(g1,g0)
    c: Coincident(g1,g-1)
    c: Angle(g-2,g1) = 1.0472
    c: Coincident(g2,g0)
    c: Diameter(g2) = 23
FEATURE [Part::Extrusion] Extrude008  label="truss_pole_extrude"
  Base = -> Sketch025
  Dir = (0,0,1)
  DirMode = 2
  FaceMakerClass = Part::FaceMakerBullseye
  FaceMakerMode = 3
  LengthFwd = 1014
  LengthRev = 0
  Placement = pos=(0,0,100) rot=(-0.32407,0.944893,0.046434;0.236492rad)
  Solid = true
  Symmetric = false
FEATURE [Sketcher::SketchObject] Sketch026  label="sling"
  ArcFitTolerance = 0
  FullyConstrained = false
  MakeInternals = false
  sketch-geometry (8):
    g0: ArcOfCircle CenterX=0 CenterY=0 CenterZ=0 NormalX=0 NormalY=0 NormalZ=1 AngleXU=0 Radius=205 StartAngle=3.18294 EndAngle=6.26636
    g1: LineSegment StartX=-204.825 StartY=-8.47479 StartZ=0 EndX=-204.825 EndY=105.407 EndZ=0
    g2: LineSegment StartX=204.971 StartY=-3.4495 StartZ=0 EndX=204.971 EndY=110.433 EndZ=0
    g3: ArcOfCircle CenterX=0 CenterY=0 CenterZ=0 NormalX=0 NormalY=0 NormalZ=1 AngleXU=0 Radius=200 StartAngle=3.16948 EndAngle=6.28413
    g4: LineSegment StartX=-199.922 StartY=-5.57575 StartZ=0 EndX=-199.922 EndY=108.306 EndZ=0
    g5: LineSegment StartX=200 StartY=0.188378 StartZ=0 EndX=200 EndY=114.07 EndZ=0
    g6: LineSegment StartX=-204.825 StartY=105.407 StartZ=0 EndX=-199.922 EndY=108.306 EndZ=0
    g7: LineSegment StartX=200 StartY=114.07 StartZ=0 EndX=204.971 EndY=110.433 EndZ=0
  constraints (20):
    c: Coincident(g0,g-1)
    c: Diameter(g0) = 410
    c: Vertical(g1)
    c: Vertical(g2)
    c: Equal(g1,g2)
    c: Distance(g1) = 113.882
    c: Coincident(g3,g0)
    c: Diameter(g3) = 400
    c: Vertical(g4)
    c: Equal(g4,g1)
    c: Vertical(g5)
    c: Equal(g5,g2)
    c: Coincident(g6,g4)
    c: Coincident(g7,g5)
    c: Coincident(g7,g2)
    c: Coincident(g2,g0)
    c: Coincident(g4,g3)
    c: Coincident(g1,g0)
    c: Coincident(g6,g1)
    c: Coincident(g5,g3)
FEATURE [Part::Extrusion] Extrude009  label="sling_extrude"
  Base = -> Sketch026
  Dir = (0,0,1)
  DirMode = 2
  FaceMakerClass = Part::FaceMakerBullseye
  FaceMakerMode = 3
  LengthFwd = 1
  LengthRev = 0
  Solid = false
  Symmetric = false
FEATURE [Sketcher::SketchObject] Sketch023  label="uta_bracket_sketch"
  ArcFitTolerance = 0
  FullyConstrained = true
  MakeInternals = false
  MapMode = 5
  expr: Constraints[13] = Constraints[12]
  expr: Constraints[1] = <<uta_ring>>.Constraints[1]
  expr: Constraints[3] = <<uta_ring>>.Constraints[3]
  expr: Constraints[4] = <<mounting_hole>>.Constraints[1]
  expr: Constraints[8] = <<mounting_hole>>.Constraints[0]
  sketch-geometry (22):
    g0: ArcOfCircle CenterX=0 CenterY=0 CenterZ=0 NormalX=0 NormalY=0 NormalZ=1 AngleXU=0 Radius=225 StartAngle=1.45386 EndAngle=1.68773
    g1: ArcOfCircle CenterX=0 CenterY=0 CenterZ=0 NormalX=0 NormalY=0 NormalZ=1 AngleXU=0 Radius=255 StartAngle=1.45386 EndAngle=1.68773
    g2: Circle CenterX=0 CenterY=240 CenterZ=0 NormalX=0 NormalY=0 NormalZ=1 AngleXU=0 Radius=3
    g3: LineSegment StartX=-29.751 StartY=253.259 StartZ=0 EndX=-26.2509 EndY=223.463 EndZ=0
    g4: LineSegment StartX=29.751 StartY=253.259 StartZ=0 EndX=26.2509 EndY=223.463 EndZ=0
    g5: LineSegment [constr] StartX=29.751 StartY=253.259 StartZ=0 EndX=-4e-16 EndY=1.6e-15 EndZ=0
    g6: LineSegment [constr] StartX=-29.751 StartY=253.259 StartZ=0 EndX=7e-16 EndY=1.5e-15 EndZ=0
    g7: ArcOfCircle [constr] CenterX=0 CenterY=0 CenterZ=0 NormalX=0 NormalY=0 NormalZ=1 AngleXU=0 Radius=240 StartAngle=1.45386 EndAngle=1.68773
    g8: LineSegment [constr] StartX=0 StartY=255 StartZ=0 EndX=0 EndY=0 EndZ=0
    g9: Circle [constr] CenterX=-15.9911 CenterY=239.467 CenterZ=0 NormalX=0 NormalY=0 NormalZ=1 AngleXU=0 Radius=10
    g10: Circle [constr] CenterX=15.9911 CenterY=239.467 CenterZ=0 NormalX=0 NormalY=0 NormalZ=1 AngleXU=0 Radius=10
    g11: Circle [constr] CenterX=0 CenterY=240 CenterZ=0 NormalX=0 NormalY=0 NormalZ=1 AngleXU=0 Radius=6
    g12: Circle [constr] CenterX=-25.375 CenterY=249.775 CenterZ=0 NormalX=0 NormalY=0 NormalZ=1 AngleXU=0 Radius=3.93965
    g13: Circle CenterX=-25.375 CenterY=249.775 CenterZ=0 NormalX=0 NormalY=0 NormalZ=1 AngleXU=0 Radius=1.5
    g14: Circle [constr] CenterX=25.375 CenterY=249.775 CenterZ=0 NormalX=0 NormalY=0 NormalZ=1 AngleXU=0 Radius=3.93965
    g15: Circle [constr] CenterX=22.9544 CenterY=227.602 CenterZ=0 NormalX=0 NormalY=0 NormalZ=1 AngleXU=0 Radius=3.75687
    g16: Circle [constr] CenterX=-22.9544 CenterY=227.602 CenterZ=0 NormalX=0 NormalY=0 NormalZ=1 AngleXU=0 Radius=3.75687
    g17: Circle CenterX=25.375 CenterY=249.775 CenterZ=0 NormalX=0 NormalY=0 NormalZ=1 AngleXU=0 Radius=1.5
    g18: Circle CenterX=22.9544 CenterY=227.602 CenterZ=0 NormalX=0 NormalY=0 NormalZ=1 AngleXU=0 Radius=1.5
    g19: Circle CenterX=-22.9544 CenterY=227.602 CenterZ=0 NormalX=0 NormalY=0 NormalZ=1 AngleXU=0 Radius=1.5
    g20: Circle CenterX=-15.9911 CenterY=239.467 CenterZ=0 NormalX=0 NormalY=0 NormalZ=1 AngleXU=0 Radius=7.5
    g21: Circle CenterX=15.9911 CenterY=239.467 CenterZ=0 NormalX=0 NormalY=0 NormalZ=1 AngleXU=0 Radius=7.5
  constraints (60):
    c: Coincident(g0,g-1)
    c: Diameter(g0) = 450
    c: Coincident(g1,g0)
    c: Diameter(g1) = 510
    c: Diameter(g2) = 6
    c: Coincident(g5,g0)
    c: Coincident(g6,g0)
    c: Coincident(g7,g0)
    c: Diameter(g7) = 480
    c: PointOnObject(g2,g7)
    c: Coincident(g8,g0)
    c: PointOnObject(g2,g8)
    c: Angle(g8,g6) = 0.116937
    c: Angle(g5,g8) = 0.116937
    c: Equal(g10,g9)
    c: Diameter(g9) = 20
    c: Coincident(g11,g2)
    c: Diameter(g11) = 12
    c: PointOnObject(g2,g-2)
    c: PointOnObject(g4,g5)
    c: PointOnObject(g0,g6)
    c: PointOnObject(g3,g6)
    c: PointOnObject(g5,g1)
    c: PointOnObject(g6,g1)
    c: PointOnObject(g8,g1)
    c: Tangent(g9,g11)
    c: Tangent(g12,g9)
    c: Tangent(g12,g1)
    c: Coincident(g13,g12)
    c: Diameter(g13) = 3
    c: Tangent(g16,g9)
    c: Tangent(g15,g10)
    c: Tangent(g14,g1)
    c: Tangent(g14,g10)
    c: Coincident(g17,g14)
    c: Coincident(g18,g15)
    c: Coincident(g19,g16)
    c: Equal(g17,g18)
    c: Equal(g18,g19)
    c: Equal(g19,g13)
    c: Coincident(g1,g4)
    c: Coincident(g3,g1)
    c: PointOnObject(g7,g5)
    c: PointOnObject(g7,g6)
    c: PointOnObject(g0,g5)
    c: Tangent(g16,g0)
    c: Tangent(g15,g0)
    c: Tangent(g14,g4)
    c: Tangent(g12,g3)
    c: Coincident(g4,g0)
    c: Coincident(g3,g0)
    c: Coincident(g21,g10)
    c: Equal(g21,g20)
    c: Diameter(g20) = 15
    c: Coincident(g20,g9)
    c: PointOnObject(g20,g7)
    c: Tangent(g16,g3)
    c: PointOnObject(g21,g7)
    c: Tangent(g15,g4)
    c: Tangent(g10,g11)
FEATURE [Part::Extrusion] Extrude010  label="upper_bracket_extrude"
  Base = -> Sketch023
  Dir = (0,0,1)
  DirMode = 2
  FaceMakerClass = Part::FaceMakerBullseye
  FaceMakerMode = 3
  LengthFwd = 4.8
  LengthRev = 0
  Solid = true
  Symmetric = false
FEATURE [PartDesign::Pocket] Pocket002  label="alignment_hole_pocket"
  BaseFeature = -> Pocket001
  Direction = (0,0,-1)
  Length = 5
  Length2 = 5
  Profile = -> Sketch013
  ReferenceAxis = -> Sketch013 [N_Axis]
  Suppressed = false
  Type = 1
FEATURE [PartDesign::PolarPattern] PolarPattern  label="mounting_holes_polar_pattern"
  Angle = 360
  Axis = -> Sketch011 [N_Axis]
  BaseFeature = -> Pocket002
  Mode = 0
  Occurrences = 12
  Offset = 120
  Originals = -> [Pocket]
  Reversed = true
  Suppressed = false
  TransformMode = 0
FEATURE [PartDesign::PolarPattern] PolarPattern001  label="weight_saving_polar_pattern1"
  Angle = 270
  Axis = -> Sketch012 [N_Axis]
  BaseFeature = -> PolarPattern
  Mode = 0
  Occurrences = 10
  Offset = 120
  Originals = -> [Pocket001]
  Suppressed = false
  TransformMode = 0
FEATURE [PartDesign::Pocket] Pocket003  label="focuser_holes"
  BaseFeature = -> PolarPattern001
  Direction = (0,0,-1)
  Length = 5
  Length2 = 5
  Profile = -> Sketch014
  ReferenceAxis = -> Sketch014 [N_Axis]
  Suppressed = false
  Type = 1
FEATURE [Sketcher::SketchObject] Sketch015  label="finder_mounting_holes"
  ArcFitTolerance = 0
  AttachmentSupport = -> [Pocket003]
  FullyConstrained = true
  MakeInternals = false
  MapMode = 5
  Placement = pos=(0,0,4.8) rot=(0,0,1;0rad)
  expr: Constraints[1] = (<<uta_ring>>.Constraints[1] + <<uta_ring>>.Constraints[3]) / 2 + 15 mm
  expr: Constraints[8] = Constraints[1] - 30 mm
  sketch-geometry (8):
    g0: Circle [constr] CenterX=-8.2e-15 CenterY=-2.48e-14 CenterZ=0 NormalX=0 NormalY=0 NormalZ=1 AngleXU=0 Radius=247.5
    g1: Circle CenterX=-180.86 CenterY=168.955 CenterZ=0 NormalX=0 NormalY=0 NormalZ=1 AngleXU=0 Radius=2
    g2: Circle CenterX=-159.09 CenterY=189.596 CenterZ=0 NormalX=0 NormalY=0 NormalZ=1 AngleXU=0 Radius=2
    g3: Circle [constr] CenterX=-8.2e-15 CenterY=-2.48e-14 CenterZ=0 NormalX=0 NormalY=0 NormalZ=1 AngleXU=0 Radius=232.5
    g4: Circle CenterX=-169.899 CenterY=158.715 CenterZ=0 NormalX=0 NormalY=0 NormalZ=1 AngleXU=0 Radius=2
    g5: Circle CenterX=-149.448 CenterY=178.105 CenterZ=0 NormalX=0 NormalY=0 NormalZ=1 AngleXU=0 Radius=2
    g6: LineSegment [constr] StartX=-180.86 StartY=168.955 StartZ=0 EndX=8e-16 EndY=-1.86e-14 EndZ=0
    g7: LineSegment [constr] StartX=-159.09 StartY=189.596 StartZ=0 EndX=-8.2e-15 EndY=-2.48e-14 EndZ=0
  constraints (20):
    c: Coincident(g0,g-1)
    c: Diameter(g0) = 495
    c: PointOnObject(g1,g0)
    c: PointOnObject(g2,g0)
    c: Equal(g2,g1)
    c: Diameter(g2) = 4
    c: Distance(g1,g2) = 30
    c: Coincident(g3,g0)
    c: Diameter(g3) = 465
    c: PointOnObject(g4,g3)
    c: PointOnObject(g5,g3)
    c: Equal(g5,g4)
    c: Equal(g4,g1)
    c: Coincident(g6,g1)
    c: Coincident(g6,g3)
    c: Coincident(g7,g2)
    c: Coincident(g7,g3)
    c: PointOnObject(g4,g6)
    c: PointOnObject(g5,g7)
    c: Angle(g-2,g7) = 0.698132
FEATURE [PartDesign::Pocket] Pocket007  label="finder_mount_holes"
  BaseFeature = -> Pocket003
  Direction = (0,0,-1)
  Length = 5
  Length2 = 5
  Profile = -> Sketch015
  ReferenceAxis = -> Sketch015 [N_Axis]
  Suppressed = false
  Type = 1
FEATURE [Part::Feature] Part__Feature  label="92095A224_Button Head Hex Drive Screw"
  Placement = pos=(240,0.5,0) rot=(0,1,0;3.14159rad)
  shape: bbox 10.5 x 10.5 x 14.58 mm, 69 faces (baked)
FEATURE [Part::FeaturePython] Array005  label="mount_screws"  # Draft array (typed FeaturePython)
  AlwaysSyncPlacement = false
  Angle = 300
  ArrayType = 1
  Axis = (0,0,1)
  Base = -> Part__Feature
  Center = (0,0,0)
  Count = 11
  ExpandArray = false
  Fuse = false
  IntervalAxis = (0,0,0)
  IntervalX = (50,0,0)
  IntervalY = (0,50,0)
  IntervalZ = (0,0,50)
  NumberCircles = 3
  NumberPolar = 11
  NumberX = 2
  NumberY = 2
  NumberZ = 1
  Placement = pos=(0,0,-3.4) rot=(0,0,1;0rad)
  PlacementList = 11 placements: [(240,0.5,0),(207.596,120.433,0),(119.567,208.096,0),(-0.5,240,0),(-120.433,207.596,0),(-208.096,119.567,0),(-240,-0.5,0),(-207.596,-120.433,0),(-119.567,-208.096,0),(0.5,-240,0),(120.433,-207.596,0)]
  RadialDistance = 50
  ScaleList = (11) [(1,1,1),(1,1,1),(1,1,1),(1,1,1),(1,1,1),(1,1,1),(1,1,1),(1,1,1),(1,1,1),(1,1,1),(1,1,1)]
  Symmetry = 1
  TangentialDistance = 25
FEATURE [Part::Feature] Part__Feature001  label="62935K17_Nylon Ribbed Knob"
  shape: bbox 27.06 x 27.06 x 18.75 mm, 75 faces (baked)
FEATURE [App::Part] _2935K17_Nylon_Ribbed_Knob  label="62935K17_Nylon Ribbed Knob002"
  Group = -> [Part__Feature001]
  Origin = -> Origin008
  Placement = pos=(0.130893,240.8,0) rot=(0,1,0;3.15905rad)
FEATURE [Part::FeaturePython] Array007  label="knobs"  # Draft array (typed FeaturePython)
  AlwaysSyncPlacement = false
  Angle = 360
  ArrayType = 1
  Axis = (0,0,1)
  Base = -> _2935K17_Nylon_Ribbed_Knob
  Center = (0,0,0)
  Count = 3
  ExpandArray = false
  Fuse = false
  IntervalAxis = (0,0,0)
  IntervalX = (50,0,0)
  IntervalY = (0,50,0)
  IntervalZ = (0,0,50)
  NumberCircles = 3
  NumberPolar = 3
  NumberX = 2
  NumberY = 2
  NumberZ = 1
  Placement = pos=(0,0,-32) rot=(0,0,1;-0.523599rad)
  PlacementList = 3 placements: [(0.130893,240.8,0),(-208.604,-120.287,0),(208.473,-120.513,0)]
  RadialDistance = 50
  ScaleList = (3) [(1,1,1),(1,1,1),(1,1,1)]
  Symmetry = 1
  TangentialDistance = 25
FEATURE [Part::Feature] Part__Feature003  label="roulement_623_2_1"
  Placement = pos=(0.915135,16.81,-33.8125) rot=(0,0,-1;1.65806rad)
  shape: bbox 11.11 x 4.9 x 10.82 mm, 14 faces (baked)
FEATURE [Part::Feature] Part__Feature004  label="roulement_623_2_2"
  Placement = pos=(0.915135,16.81,-33.8125) rot=(0,0,-1;1.65806rad)
  shape: bbox 6.543 x 4.438 x 6.429 mm, 8 faces (baked)
FEATURE [Part::Feature] Part__Feature005  label="roulement_623_2_3"
  Placement = pos=(0.915135,16.81,-33.8125) rot=(0,0,-1;1.65806rad)
  shape: bbox 7.212 x 2.08 x 7.379 mm, 14 faces (baked)
FEATURE [App::Part] roulement_623_2
  Group = -> [Part__Feature003,Part__Feature004,Part__Feature005]
  Origin = -> Origin009
FEATURE [App::Part] bearing_623_2_v1  label="bearing_623_2 v1"
  Group = -> [roulement_623_2]
  Origin = -> Origin010
FEATURE [Part::Feature] Part__Feature006  label="din_433-2_3_2_300_hv v1"
  Placement = pos=(-29.5657,12.8253,16.4156) rot=(0.999486,0.023501,0.021788;1.49569rad)
  shape: bbox 6.016 x 1.021 x 6.021 mm, 6 faces (baked)
FEATURE [Part::Feature] Part__Feature007  label="din_433-2_3_2_300_hv v002"
  Placement = pos=(-28.9992,-0.125266,17.3969) rot=(-0.999558,-0.020201,0.02179;1.64686rad)
  shape: bbox 6.016 x 1.021 x 6.021 mm, 6 faces (baked)
FEATURE [Part::Feature] Part__Feature008  label="din_433-2_3_2_300_hv v003"
  Placement = pos=(-0.566512,-0.125266,-33.8125) rot=(-0.998099,0.043578,-0.043578;1.5727rad)
  shape: bbox 6.021 x 1.021 x 6 mm, 6 faces (baked)
FEATURE [Part::Feature] Part__Feature009  label="din_433-2_3_2_300_hv v004"
  Placement = pos=(0.566512,12.8253,-33.8125) rot=(0.998099,-0.043578,-0.043578;1.5727rad)
  shape: bbox 6.021 x 1.021 x 6 mm, 6 faces (baked)
FEATURE [Part::Feature] Part__Feature010  label="roulement_623_2_004"
  Placement = pos=(-0.915135,-4.11004,-13.8125) rot=(0,0,1;1.48353rad)
  shape: bbox 11.11 x 4.9 x 10.82 mm, 14 faces (baked)
FEATURE [Part::Feature] Part__Feature011  label="roulement_623_2_005"
  Placement = pos=(-0.915135,-4.11004,-13.8125) rot=(0,0,1;1.48353rad)
  shape: bbox 6.543 x 4.438 x 6.429 mm, 8 faces (baked)
FEATURE [Part::Feature] Part__Feature012  label="roulement_623_2_006"
  Placement = pos=(-0.915135,-4.11004,-13.8125) rot=(0,0,1;1.48353rad)
  shape: bbox 7.212 x 2.08 x 7.379 mm, 14 faces (baked)
FEATURE [App::Part] roulement_623_003
  Group = -> [Part__Feature010,Part__Feature011,Part__Feature012]
  Origin = -> Origin011
FEATURE [App::Part] bearing_623_2_v002  label="bearing_623_2 v002"
  Group = -> [roulement_623_003]
  Origin = -> Origin012
  Placement = pos=(0,0,-20) rot=(0,0,1;0rad)
FEATURE [Part::Feature] Part__Feature013  label="roulement_623_2_007"
  Placement = pos=(-10.7401,16.81,16.1137) rot=(-0.039457,-0.037773,-0.998507;1.5287rad)
  shape: bbox 10.97 x 4.868 x 11.07 mm, 14 faces (baked)
FEATURE [Part::Feature] Part__Feature014  label="roulement_623_2_008"
  Placement = pos=(-10.7401,16.81,16.1137) rot=(-0.039457,-0.037773,-0.998507;1.5287rad)
  shape: bbox 6.493 x 4.438 x 6.531 mm, 8 faces (baked)
FEATURE [Part::Feature] Part__Feature015  label="roulement_623_2_009"
  Placement = pos=(-10.7401,16.81,16.1137) rot=(-0.039457,-0.037773,-0.998507;1.5287rad)
  shape: bbox 7.229 x 2.091 x 7.363 mm, 14 faces (baked)
FEATURE [App::Part] roulement_623_004
  Group = -> [Part__Feature013,Part__Feature014,Part__Feature015]
  Origin = -> Origin013
FEATURE [App::Part] bearing_623_2_v003  label="bearing_623_2 v003"
  Group = -> [roulement_623_004]
  Origin = -> Origin014
  Placement = pos=(-19,0,0) rot=(0,0,1;0rad)
FEATURE [Part::Feature] Part__Feature016  label="roulement_623_2_010"
  Placement = pos=(-12.8249,-4.11004,17.6988) rot=(-0.036166,0.037778,0.998632;1.61576rad)
  shape: bbox 10.97 x 4.868 x 11.07 mm, 14 faces (baked)
FEATURE [Part::Feature] Part__Feature017  label="roulement_623_2_011"
  Placement = pos=(-12.8249,-4.11004,17.6988) rot=(-0.036166,0.037778,0.998632;1.61576rad)
  shape: bbox 6.493 x 4.438 x 6.531 mm, 8 faces (baked)
FEATURE [Part::Feature] Part__Feature018  label="roulement_623_2_012"
  Placement = pos=(-12.8249,-4.11004,17.6988) rot=(-0.036166,0.037778,0.998632;1.61576rad)
  shape: bbox 7.229 x 2.091 x 7.363 mm, 14 faces (baked)
FEATURE [App::Part] roulement_623_005
  Group = -> [Part__Feature016,Part__Feature017,Part__Feature018]
  Origin = -> Origin015
FEATURE [App::Part] bearing_623_2_v004  label="bearing_623_2 v004"
  Group = -> [roulement_623_005]
  Origin = -> Origin016
  Placement = pos=(-16,0,0) rot=(0,0,1;0rad)
FEATURE [Part::Feature] Part__Feature019  label="din_912-m3x0_5-25-c3 v1"
  Placement = pos=(-29.7401,16.81,16.1137) rot=(-0.999558,-0.020201,0.02179;1.64686rad)
  shape: bbox 5.948 x 28.23 x 6.536 mm, 17 faces (baked)
FEATURE [Part::Feature] Part__Feature020  label="din_912-m3x0_5-25-c3 v002"
  Placement = pos=(0.915135,16.81,-33.8125) rot=(-0.998099,0.043578,-0.043578;1.5727rad)
  shape: bbox 6.852 x 28.23 x 5.953 mm, 17 faces (baked)
FEATURE [Part::Feature] Part__Feature021  label="nut_din934_m3-8 v1"
  Placement = pos=(-0.915135,-4.11004,-33.8125) rot=(0.998099,-0.043578,-0.043578;1.5727rad)
  shape: bbox 6.498 x 2.902 x 6.351 mm, 13 faces (baked)
FEATURE [Part::Feature] Part__Feature022  label="nut_din934_m3-8 v002"
  Placement = pos=(-28.8249,-4.11004,17.6988) rot=(0.999486,0.023501,0.021788;1.49569rad)
  shape: bbox 6.43 x 2.903 x 6.481 mm, 13 faces (baked)
FEATURE [Part::Feature] Part__Feature023  label="Kartelschroef M4 lang kunststof v2"
  Placement = pos=(33.3159,21.84,-0.497356) rot=(-0.583096,-0.574456,-0.574456;2.0858rad)
  shape: bbox 21.36 x 10.02 x 10.12 mm, 152 faces (baked)
FEATURE [Part::Feature] Part__Feature024  label="Component1"
  Placement = pos=(0,-35.16,0) rot=(0,-1,0;1.55587rad)
  shape: bbox 59.03 x 61.5 x 59 mm, 7 faces (baked)
FEATURE [Part::Feature] Part__Feature025  label="Kartelschroef M4 lang v2"
  Placement = pos=(34.3805,6.35,19.8496) rot=(0.694747,0.694747,0.186157;2.77349rad)
  shape: bbox 21.15 x 10.02 x 15.89 mm, 152 faces (baked)
FEATURE [Part::Feature] Part__Feature026  label="SOLID"
  shape: bbox 75.25 x 13 x 75.25 mm, 20 faces (baked)
FEATURE [App::Part] HC_2_v9  label="HC-2 v9"
  Group = -> [bearing_623_2_v1,Part__Feature006,Part__Feature007,Part__Feature008,Part__Feature009,bearing_623_2_v002,bearing_623_2_v003,bearing_623_2_v004,Part__Feature019,Part__Feature020,Part__Feature021,Part__Feature022,Part__Feature023,Part__Feature024,Part__Feature025,Part__Feature026]
  Origin = -> Origin017
  Placement = pos=(0,9,0) rot=(0,0,1;0rad)
FEATURE [Part::Sphere] Sphere
  Angle1 = -90
  Angle2 = 90
  Angle3 = 360
  AttacherType = Attacher::AttachEngine3D
  Placement = pos=(-16,240,-7) rot=(0,0,1;0rad)
  Radius = 10
FEATURE [Part::FeaturePython] Array011  label="ball_pair"  # Draft array (typed FeaturePython)
  AlwaysSyncPlacement = false
  Angle = -7.6
  ArrayType = 1
  Axis = (0,0,1)
  Base = -> Sphere
  Center = (0,0,0)
  Count = 2
  ExpandArray = false
  Fuse = false
  IntervalAxis = (0,0,0)
  IntervalX = (50,0,0)
  IntervalY = (0,50,0)
  IntervalZ = (0,0,50)
  NumberCircles = 3
  NumberPolar = 2
  NumberX = 2
  NumberY = 2
  NumberZ = 1
  PlacementList = 2 placements: [(-16,240,-7),(15.8821,240.008,-7)]
  RadialDistance = 50
  ScaleList = (2) [(1,1,1),(1,1,1)]
  Symmetry = 1
  TangentialDistance = 25
FEATURE [Part::Mirroring] Part__Mirroring003  label="truss_pole_extrude (Mirror #4)"
  Base = (0,0,0)
  Normal = (1,0,0)
  Source = -> Extrude008
FEATURE [Sketcher::SketchObject] Sketch027  label="secondary_mirror_sketch"
  ArcFitTolerance = 0
  FullyConstrained = true
  MakeInternals = false
  Placement = pos=(0,-5,0) rot=(1,0,0;0.785398rad)
  expr: Constraints[6] = Constraints[5] * 2 / 1.4142
  sketch-geometry (5):
    g0: Ellipse CenterX=0 CenterY=0 CenterZ=0 NormalX=0 NormalY=0 NormalZ=1 MajorRadius=62.8624 MinorRadius=44.45 AngleXU=1.5708
    g1: LineSegment [constr] StartX=0 StartY=62.8624 StartZ=0 EndX=0 EndY=-62.8624 EndZ=0
    g2: LineSegment [constr] StartX=-44.45 StartY=0 StartZ=0 EndX=44.45 EndY=0 EndZ=0
    g3: GeomPoint [constr] X=4.9e-15 Y=44.4509 Z=0
    g4: GeomPoint [constr] X=0 Y=-44.4509 Z=0
  constraints (5):
    c: InternalAlignment(g1-g4 -> g0) x4
    c: Coincident(g0,g-1)
    c: Distance(g2) = 88.9
    c: Distance(g1) = 125.725
    c: Parallel(g-2,g1)
FEATURE [Part::Extrusion] Extrude011  label="secondary_mirror"
  Base = -> Sketch027
  Dir = (0,0,1)
  DirMode = 0
  FaceMakerClass = Part::FaceMakerBullseye
  FaceMakerMode = 3
  LengthFwd = 20
  LengthRev = 0
  Placement = pos=(0,0,61.5) rot=(0,0,1;0.366519rad)
  Solid = true
  Symmetric = false
FEATURE [Sketcher::SketchObject] Sketch005  label="spider_hub_sketch"
  ArcFitTolerance = 0
  AttachmentOffset = pos=(0,0,50) rot=(0,0,1;0rad)
  FullyConstrained = true
  MakeInternals = false
  MapMode = 5
  expr: Constraints[10] = (<<uta_ring>>.Constraints[1] + <<uta_ring>>.Constraints[3]) / 2
  sketch-geometry (17):
    g0: Circle [constr] CenterX=0 CenterY=0 CenterZ=0 NormalX=0 NormalY=0 NormalZ=1 AngleXU=0 Radius=42.5
    g1: LineSegment [constr] StartX=-207.846 StartY=120 StartZ=0 EndX=4.62e-14 EndY=-240 EndZ=0
    g2: LineSegment [constr] StartX=4.62e-14 StartY=-240 StartZ=0 EndX=207.846 EndY=120 EndZ=0
    g3: LineSegment [constr] StartX=207.846 StartY=120 StartZ=0 EndX=-207.846 EndY=120 EndZ=0
    g4: Circle [constr] CenterX=0 CenterY=0 CenterZ=0 NormalX=0 NormalY=0 NormalZ=1 AngleXU=0 Radius=240
    g5: LineSegment [constr] StartX=-207.846 StartY=120 StartZ=0 EndX=-1.78e-14 EndY=1.42e-14 EndZ=0
    g6: LineSegment [constr] StartX=207.846 StartY=120 StartZ=0 EndX=-1.09e-14 EndY=-9e-16 EndZ=0
    g7: LineSegment [constr] StartX=4.62e-14 StartY=-240 StartZ=0 EndX=0 EndY=0 EndZ=0
    g8: Circle CenterX=0 CenterY=0 CenterZ=0 NormalX=0 NormalY=0 NormalZ=1 AngleXU=0 Radius=5
    g9: LineSegment [constr] StartX=-23.8157 StartY=13.75 StartZ=0 EndX=7.7e-15 EndY=-27.5 EndZ=0
    g10: LineSegment [constr] StartX=7.7e-15 StartY=-27.5 StartZ=0 EndX=23.8157 EndY=13.75 EndZ=0
    g11: LineSegment [constr] StartX=23.8157 StartY=13.75 StartZ=0 EndX=-23.8157 EndY=13.75 EndZ=0
    g12: Circle [constr] CenterX=0 CenterY=0 CenterZ=0 NormalX=0 NormalY=0 NormalZ=1 AngleXU=0 Radius=27.5
    g13: Circle CenterX=23.8157 CenterY=13.75 CenterZ=0 NormalX=0 NormalY=0 NormalZ=1 AngleXU=0 Radius=2.5
    g14: Circle CenterX=7.7e-15 CenterY=-27.5 CenterZ=0 NormalX=0 NormalY=0 NormalZ=1 AngleXU=0 Radius=2.5
    g15: Circle CenterX=-23.8157 CenterY=13.75 CenterZ=0 NormalX=0 NormalY=0 NormalZ=1 AngleXU=0 Radius=2.5
    g16: Circle CenterX=0 CenterY=0 CenterZ=0 NormalX=0 NormalY=0 NormalZ=1 AngleXU=0 Radius=37.5
  constraints (40):
    c: Coincident(g0,g-1)
    c: Coincident(g1,g2)
    c: Coincident(g2,g3)
    c: Coincident(g3,g1)
    c: Equal(g1,g2)
    c: Equal(g1,g3)
    c: PointOnObject(g1,g4)
    c: PointOnObject(g2,g4)
    c: PointOnObject(g3,g4)
    c: Coincident(g4,g0)
    c: Diameter(g4) = 480
    c: Coincident(g5,g1)
    c: Coincident(g6,g2)
    c: Coincident(g7,g1)
    c: Diameter(g0) = 85
    c: Parallel(g3,g-1)
    c: Diameter(g8) = 10
    c: Coincident(g9,g10)
    c: Coincident(g10,g11)
    c: Coincident(g11,g9)
    c: Equal(g9,g10)
    c: Equal(g9,g11)
    c: PointOnObject(g9,g12)
    c: PointOnObject(g10,g12)
    c: PointOnObject(g11,g12)
    c: Coincident(g13,g10)
    c: Diameter(g13) = 5
    c: Coincident(g14,g9)
    c: Coincident(g15,g9)
    c: Equal(g15,g14)
    c: Equal(g14,g13)
    c: Diameter(g12) = 55
    c: Diameter(g16) = 75
    c: Coincident(g7,g6)
    c: Coincident(g7,g5)
    c: Coincident(g7,g8)
    c: Coincident(g8,g16)
    c: Coincident(g8,g0)
    c: Coincident(g12,g8)
    c: PointOnObject(g14,g7)
FEATURE [Part::Extrusion] Extrude013  label="spider_hub_extrude"
  Base = -> Sketch005
  Dir = (0,0,1)
  DirMode = 2
  FaceMakerClass = Part::FaceMakerBullseye
  FaceMakerMode = 3
  LengthFwd = 15
  LengthRev = 0
  Placement = pos=(0,0,135.5) rot=(0,0,-1;0.523599rad)
  Solid = true
  Symmetric = false
FEATURE [PartDesign::PolarPattern] PolarPattern002  label="bracket_alignment_holes"
  Angle = 300
  Axis = -> Sketch013 [N_Axis]
  BaseFeature = -> Pocket007
  Mode = 0
  Occurrences = 11
  Offset = 120
  Originals = -> [Pocket002]
  Suppressed = false
  TransformMode = 0
FEATURE [PartDesign::Body] Body  label="uta_ring_body"
  AllowCompound = false
  Group = -> [Sketch010,Pad,Sketch011,Pocket,Sketch012,Pocket001,Sketch013,Pocket002,PolarPattern,PolarPattern001,Sketch014,Pocket003,Sketch015,Pocket007,PolarPattern002]
  Origin = -> Origin
  Tip = -> PolarPattern002
FEATURE [Sketcher::SketchObject] Sketch028  label="vane_sketch"
  ArcFitTolerance = 0
  FullyConstrained = true
  MakeInternals = false
  Placement = pos=(-1,0,0) rot=(0.57735,0.57735,0.57735;2.0944rad)
  expr: Constraints[24] = <<spider_hub_sketch>>.Constraints[32] / 2
  sketch-geometry (10):
    g0: LineSegment StartX=18 StartY=129 StartZ=0 EndX=18 EndY=114 EndZ=0
    g1: LineSegment StartX=43.2158 StartY=129 StartZ=0 EndX=249 EndY=21 EndZ=0
    g2: LineSegment StartX=49.076 StartY=97.6906 StartZ=0 EndX=223.784 EndY=6 EndZ=0
    g3: LineSegment StartX=249 StartY=21 StartZ=0 EndX=249 EndY=6 EndZ=0
    g4: Circle CenterX=240 CenterY=15 CenterZ=0 NormalX=0 NormalY=0 NormalZ=1 AngleXU=0 Radius=3
    g5: LineSegment StartX=223.784 StartY=6 StartZ=0 EndX=249 EndY=6 EndZ=0
    g6: Circle [constr] CenterX=240 CenterY=15 CenterZ=0 NormalX=0 NormalY=0 NormalZ=1 AngleXU=0 Radius=9
    g7: LineSegment StartX=43.2158 StartY=129 StartZ=0 EndX=18 EndY=129 EndZ=0
    g8: LineSegment StartX=18 StartY=114 StartZ=0 EndX=37.5 EndY=114 EndZ=0
    g9: LineSegment StartX=37.5 StartY=114 StartZ=0 EndX=49.076 EndY=97.6906 EndZ=0
  constraints (29):
    c: Coincident(g3,g1)
    c: Parallel(g0,g3)
    c: Parallel(g3,g-2)
    c: Parallel(g1,g2)
    c: Distance(g0,g1) = 25
    c: DistanceY(g-1,g0) = 114
    c: DistanceX(g-2,g0) = 18
    c: Diameter(g4) = 6
    c: DistanceX(g-2,g4) = 240
    c: Horizontal(g5)
    c: Coincident(g2,g5)
    c: Coincident(g3,g5)
    c: DistanceY(g-1,g4) = 15
    c: Coincident(g6,g4)
    c: Tangent(g6,g3)
    c: Diameter(g6) = 18
    c: Horizontal(g7)
    c: Coincident(g0,g7)
    c: Coincident(g1,g7)
    c: Distance(g0) = 15
    c: Tangent(g5,g6)
    c: Equal(g3,g0)
    c: Coincident(g8,g0)
    c: Horizontal(g8)
    c: DistanceX(g-2,g8) = 37.5
    c: Coincident(g9,g8)
    c: Coincident(g2,g9)
    c: PointOnObject(g0,g2)
    c: Distance(g9) = 20
FEATURE [Part::Extrusion] Extrude012  label="vane"
  Base = -> Sketch028
  Dir = (1,0,0)
  DirMode = 2
  FaceMakerClass = Part::FaceMakerBullseye
  FaceMakerMode = 3
  LengthFwd = 3
  LengthRev = 0
  Placement = pos=(0,0,21.6) rot=(0,0,1;0rad)
  Solid = true
  Symmetric = false
FEATURE [Part::FeaturePython] Array013  label="vanes"  # Draft array (typed FeaturePython)
  AlwaysSyncPlacement = false
  Angle = 360
  ArrayType = 1
  Axis = (0,0,1)
  Base = -> Extrude012
  Center = (0,0,0)
  Count = 3
  ExpandArray = false
  Fuse = false
  IntervalAxis = (0,0,0)
  IntervalX = (50,0,0)
  IntervalY = (0,50,0)
  IntervalZ = (0,0,50)
  NumberCircles = 3
  NumberPolar = 3
  NumberX = 2
  NumberY = 2
  NumberZ = 1
  Placement = pos=(0,0,0) rot=(0,0,-1;0.593412rad)
  PlacementList = 3 placements: [(0,0,21.6),(0,0,21.6),(0,0,21.6)]
  RadialDistance = 50
  ScaleList = (3) [(1,1,1),(1,1,1),(1,1,1)]
  Symmetry = 1
  TangentialDistance = 25
FEATURE [Part::Cut] Cut  label="hub"
  Base = -> Extrude013
  Tool = -> Array013
FEATURE [Sketcher::SketchObject] Sketch029  label="secondary_stalk_sketch"
  ArcFitTolerance = 0
  FullyConstrained = true
  MakeInternals = false
  sketch-geometry (2):
    g0: Circle CenterX=0 CenterY=0 CenterZ=0 NormalX=0 NormalY=0 NormalZ=1 AngleXU=0 Radius=32.5
    g1: Circle CenterX=0 CenterY=0 CenterZ=0 NormalX=0 NormalY=0 NormalZ=1 AngleXU=0 Radius=4.25
  constraints (4):
    c: Coincident(g0,g-1)
    c: Diameter(g0) = 65
    c: Coincident(g1,g0)
    c: Diameter(g1) = 8.5
FEATURE [Part::Extrusion] Extrude014  label="stalk"
  Base = -> Sketch029
  Dir = (0,0,-1)
  DirMode = 0
  FaceMakerClass = Part::FaceMakerBullseye
  FaceMakerMode = 3
  LengthFwd = 90
  LengthRev = 0
  Placement = pos=(0,0,119.5) rot=(0,0,1;0rad)
  Solid = true
  Symmetric = false
FEATURE [Part::FeaturePython] Slice  # WARN: FeaturePython — macro-defined, semantics opaque (R4)
  Base = -> Extrude014
  Mode = 1
  Tolerance = 0
  Tools = -> [Extrude011]
FEATURE [Part::FeaturePython] Slice_child0  label="stalk_slice"  # WARN: FeaturePython — macro-defined, semantics opaque (R4)
  Base = -> Slice
  FilterType = 1
  Invert = false
  OverrideMaxVal = 0
  WindowFrom = 80
  WindowTo = 100
  items = 0
FEATURE [Sketcher::SketchObject] Sketch030  label="spider_hub_plate_clutch"
  ArcFitTolerance = 0
  FullyConstrained = true
  MakeInternals = false
  MapMode = 1
  expr: Constraints[1] = <<secondary_stalk_sketch>>.Constraints[1]
  expr: Constraints[3] = <<spider_hub_sketch>>.Constraints[16]
  sketch-geometry (2):
    g0: Circle CenterX=0 CenterY=0 CenterZ=0 NormalX=0 NormalY=0 NormalZ=1 AngleXU=0 Radius=32.5
    g1: Circle CenterX=0 CenterY=0 CenterZ=0 NormalX=0 NormalY=0 NormalZ=1 AngleXU=0 Radius=5
  constraints (4):
    c: Coincident(g0,g-1)
    c: Diameter(g0) = 65
    c: Coincident(g1,g0)
    c: Diameter(g1) = 10
FEATURE [Part::Extrusion] Extrude015  label="spider_hub_plate_clutch_extrude"
  Base = -> Sketch030
  Dir = (0,0,1)
  DirMode = 2
  FaceMakerClass = Part::FaceMakerBullseye
  FaceMakerMode = 3
  LengthFwd = 2
  LengthRev = 0
  Placement = pos=(0,0,119) rot=(0,0,1;0rad)
  Solid = true
  Symmetric = false
FEATURE [App::Part] Part001  label="focuser_assembly"
  Group = -> [Body007,HC_2_v9]
  Origin = -> Origin019
  Placement = pos=(-87.5,228,61) rot=(0,0,1;0.366519rad)
FEATURE [Part::FeaturePython] Array016  label="rings"  # Draft array (typed FeaturePython)
  AlwaysSyncPlacement = false
  Angle = 360
  ArrayType = 0
  Axis = (0,0,1)
  Base = -> Body
  Center = (0,0,0)
  Count = 2
  ExpandArray = false
  Fuse = false
  IntervalAxis = (0,0,0)
  IntervalX = (100,0,0)
  IntervalY = (0,100,0)
  IntervalZ = (0,0,16.8)
  NumberCircles = 3
  NumberPolar = 5
  NumberX = 1
  NumberY = 1
  NumberZ = 2
  PlacementList = 2 placements: [(0,0,0),(0,0,16.8)]
  RadialDistance = 50
  ScaleList = (2) [(1,1,1),(1,1,1)]
  Symmetry = 1
  TangentialDistance = 25
FEATURE [Part::FeaturePython] Clone006  label="mount_screws_mirrored"  # Draft clone (typed FeaturePython)
  AttacherType = Attacher::AttachEngine3D
  Fuse = false
  Objects = -> [Array005]
  Placement = pos=(0,0,24.9) rot=(0,1,0;3.14159rad)
  Scale = (1,1,1)
FEATURE [App::Part] Part005  label="uta_screws"
  Group = -> [Clone006,Part__Feature,Array005]
  Origin = -> Origin023
FEATURE [App::Part] Part006  label="truss_pair"
  Group = -> [Sketch025,Extrude008,Part__Mirroring003]
  Origin = -> Origin024
FEATURE [Part::FeaturePython] Array009  label="trusses"  # Draft array (typed FeaturePython)
  AlwaysSyncPlacement = false
  Angle = 360
  ArrayType = 1
  Axis = (0,0,1)
  Base = -> Part006
  Center = (0,0,0)
  Count = 3
  ExpandArray = false
  Fuse = false
  IntervalAxis = (0,0,0)
  IntervalX = (50,0,0)
  IntervalY = (0,50,0)
  IntervalZ = (0,0,50)
  NumberCircles = 3
  NumberPolar = 3
  NumberX = 2
  NumberY = 2
  NumberZ = 1
  PlacementList = 3 placements: [(0,0,0),(0,0,0),(0,0,0)]
  RadialDistance = 50
  ScaleList = (3) [(1,1,1),(1,1,1),(1,1,1)]
  Symmetry = 1
  TangentialDistance = 25
FEATURE [Part::FeaturePython] Array  # Draft array (typed FeaturePython)
  AlwaysSyncPlacement = false
  Angle = 360
  ArrayType = 0
  Axis = (0,0,1)
  Base = -> Extrude003
  Center = (0,0,0)
  Count = 2
  ExpandArray = false
  Fuse = false
  IntervalAxis = (0,0,0)
  IntervalX = (100,0,0)
  IntervalY = (0,-170.82,0)
  IntervalZ = (0,0,100)
  NumberCircles = 3
  NumberPolar = 5
  NumberX = 1
  NumberY = 2
  NumberZ = 1
  PlacementList = 2 placements: [(0,0,-37),(0,-170.82,-37)]
  RadialDistance = 50
  ScaleList = (2) [(1,1,1),(1,1,1)]
  Symmetry = 1
  TangentialDistance = 25
FEATURE [App::Part] Part009  label="cell_frame"
  Group = -> [Part__Mirroring,Sketch007,Sketch,Extrude003,Extrude004,Array]
  Origin = -> Origin027
FEATURE [Part::Mirroring] Part__Mirroring004  label="triangle_extrude (Mirror #5)"
  Base = (0,0,0)
  Normal = (1,0,0)
  Source = -> Extrude
FEATURE [App::Part] Part008  label="mirror_cell_rocker"
  Group = -> [Sketch001,Extrude,Sketch002,Extrude001,Part__Mirroring004]
  Origin = -> Origin026
FEATURE [Part::FeaturePython] Array017  label="mirror_cell_rockers"  # Draft array (typed FeaturePython)
  AlwaysSyncPlacement = false
  Angle = 360
  ArrayType = 1
  Axis = (0,0,1)
  Base = -> Part008
  Center = (0,0,0)
  Count = 3
  ExpandArray = false
  Fuse = false
  IntervalAxis = (0,0,0)
  IntervalX = (50,0,0)
  IntervalY = (0,50,0)
  IntervalZ = (0,0,50)
  NumberCircles = 3
  NumberPolar = 3
  NumberX = 2
  NumberY = 2
  NumberZ = 1
  PlacementList = 3 placements: [(0,0,0),(0,0,0),(0,0,0)]
  RadialDistance = 50
  ScaleList = (3) [(1,1,1),(1,1,1),(1,1,1)]
  Symmetry = 1
  TangentialDistance = 25
FEATURE [App::Part] Part010  label="mirror_back_support"
  Group = -> [Part008,Array017,Sketch006,Extrude006]
  Origin = -> Origin028
FEATURE [App::Part] Part011  label="mirror_edge_support"
  Group = -> [Sketch026,Extrude009,Sketch008,Extrude005,Part__Mirroring001]
  Origin = -> Origin029
FEATURE [Sketcher::SketchObject] Sketch031  label="lta_truss_bracket_sketch"
  ArcFitTolerance = 0
  FullyConstrained = false
  MakeInternals = false
  Placement = pos=(0,0,0) rot=(1,0,0;3.14159rad)
  expr: Constraints[3] = Sketch023.Constraints[14]
  sketch-geometry (20):
    g0: Circle CenterX=63.7597 CenterY=32.4089 CenterZ=0 NormalX=0 NormalY=0 NormalZ=1 AngleXU=0 Radius=0
    g1: Circle CenterX=95.7397 CenterY=32.4089 CenterZ=0 NormalX=0 NormalY=0 NormalZ=1 AngleXU=0 Radius=0
    g2: LineSegment [constr] StartX=63.7597 StartY=32.4089 StartZ=0 EndX=95.7397 EndY=32.4089 EndZ=0
    g3: LineSegment StartX=64.2597 StartY=47.4089 StartZ=0 EndX=95.2397 EndY=47.4089 EndZ=0
    g4: LineSegment StartX=107.74 StartY=34.9089 StartZ=0 EndX=107.74 EndY=29.9089 EndZ=0
    g5: LineSegment StartX=95.2397 StartY=17.4089 StartZ=0 EndX=64.2597 EndY=17.4089 EndZ=0
    g6: LineSegment StartX=51.7597 StartY=29.9089 StartZ=0 EndX=51.7597 EndY=34.9089 EndZ=0
    g7: LineSegment [constr] StartX=79.7497 StartY=47.4089 StartZ=0 EndX=79.7497 EndY=17.4089 EndZ=0
    g8: Circle CenterX=57.7597 CenterY=32.4089 CenterZ=0 NormalX=0 NormalY=0 NormalZ=1 AngleXU=0 Radius=3
    g9: Circle CenterX=101.74 CenterY=32.4089 CenterZ=0 NormalX=0 NormalY=0 NormalZ=1 AngleXU=0 Radius=3
    g10: Circle [constr] CenterX=57.7597 CenterY=32.4089 CenterZ=0 NormalX=0 NormalY=0 NormalZ=1 AngleXU=0 Radius=6
    g11: ArcOfCircle CenterX=64.2597 CenterY=29.9089 CenterZ=0 NormalX=0 NormalY=0 NormalZ=1 AngleXU=0 Radius=12.5 StartAngle=3.14159 EndAngle=4.71239
    g12: GeomPoint [constr] X=51.7597 Y=17.4089 Z=0
    g13: ArcOfCircle CenterX=64.2597 CenterY=34.9089 CenterZ=0 NormalX=0 NormalY=0 NormalZ=1 AngleXU=0 Radius=12.5 StartAngle=1.5708 EndAngle=3.14159
    g14: GeomPoint [constr] X=51.7597 Y=47.4089 Z=0
    g15: ArcOfCircle CenterX=95.2397 CenterY=34.9089 CenterZ=0 NormalX=0 NormalY=0 NormalZ=1 AngleXU=0 Radius=12.5 StartAngle=-9e-16 EndAngle=1.5708
    g16: GeomPoint [constr] X=107.74 Y=47.4089 Z=0
    g17: ArcOfCircle CenterX=95.2397 CenterY=29.9089 CenterZ=0 NormalX=0 NormalY=0 NormalZ=1 AngleXU=0 Radius=12.5 StartAngle=4.71239 EndAngle=6.28319
    g18: GeomPoint [constr] X=107.74 Y=17.4089 Z=0
    g19: Circle CenterX=79.7497 CenterY=32.4089 CenterZ=0 NormalX=0 NormalY=0 NormalZ=1 AngleXU=0 Radius=3
  constraints (45):
    c: Coincident(g2,g0)
    c: Coincident(g2,g1)
    c: Equal(g0,g1)
    c: Diameter(g0) = 0
    c: Distance(g2) = 31.98
    c: Horizontal(g3)
    c: Horizontal(g5)
    c: Vertical(g6)
    c: Symmetric(g16,g18,g2)
    c: PointOnObject(g7,g3)
    c: PointOnObject(g7,g5)
    c: Symmetric(g14,g16,g7)
    c: Symmetric(g0,g1,g7)
    c: Distance(g14,g12) = 30
    c: PointOnObject(g8,g2)
    c: Equal(g8,g9)
    c: Symmetric(g8,g9,g7)
    c: Diameter(g8) = 6
    c: Coincident(g10,g8)
    c: Diameter(g10) = 12
    c: Tangent(g10,g6)
    c: Tangent(g10,g0)
    c: PointOnObject(g12,g6)
    c: PointOnObject(g12,g5)
    c: Tangent(g6,g11) = 1.5708
    c: Tangent(g5,g11) = 1.5708
    c: PointOnObject(g14,g6)
    c: PointOnObject(g14,g3)
    c: Tangent(g6,g13) = 1.5708
    c: Tangent(g3,g13) = 1.5708
    c: PointOnObject(g16,g3)
    c: PointOnObject(g16,g4)
    c: Tangent(g3,g15) = 1.5708
    c: Tangent(g4,g15) = 1.5708
    c: PointOnObject(g18,g5)
    c: PointOnObject(g18,g4)
    c: Tangent(g5,g17) = 1.5708
    c: Tangent(g4,g17) = 1.5708
    c: Equal(g11,g13)
    c: Equal(g13,g15)
    c: Equal(g15,g17)
    c: Diameter(g13) = 25
    c: PointOnObject(g19,g2)
    c: Equal(g19,g9)
    c: PointOnObject(g19,g7)
FEATURE [Part::Extrusion] Extrude016  label="lta_truss_bracket"
  Base = -> Sketch031
  Dir = (0,0,-1)
  DirMode = 2
  FaceMakerClass = Part::FaceMakerBullseye
  FaceMakerMode = 3
  LengthFwd = 4.8
  LengthRev = 0
  Solid = true
  Symmetric = false
FEATURE [App::Part] Part007  label="lta"
  Group = -> [Sketch003,Extrude002,Part009,Sketch009,Extrude007,Part__Mirroring002,Part010,Part011,Sketch031,Extrude016]
  Origin = -> Origin025
FEATURE [Sketcher::SketchObject] Sketch032
  ArcFitTolerance = 0
  FullyConstrained = true
  MakeInternals = false
  Placement = pos=(0,0,0) rot=(1,0,0;1.5708rad)
  expr: Constraints[12] = 25 / 2
  expr: Constraints[8] = (23 - 0.2) / 2
  sketch-geometry (18):
    g0: LineSegment StartX=-11.4 StartY=30 StartZ=0 EndX=-12.5 EndY=30 EndZ=0
    g1: LineSegment StartX=-12.5 StartY=30 StartZ=0 EndX=-6 EndY=50 EndZ=0
    g2: LineSegment StartX=-6 StartY=50 StartZ=0 EndX=0 EndY=50 EndZ=0
    g3: LineSegment StartX=0 StartY=50 StartZ=0 EndX=0 EndY=0 EndZ=0
    g4: LineSegment StartX=0 StartY=0 StartZ=0 EndX=-11.4 EndY=0 EndZ=0
    g5: LineSegment StartX=-11.4 StartY=30 StartZ=0 EndX=-11.4 EndY=23.625 EndZ=0
    g6: LineSegment StartX=-11.4 StartY=23.625 StartZ=0 EndX=-10.4 EndY=23.625 EndZ=0
    g7: LineSegment StartX=-10.4 StartY=23.625 StartZ=0 EndX=-10.4 EndY=22.125 EndZ=0
    g8: LineSegment StartX=-10.4 StartY=22.125 StartZ=0 EndX=-11.4 EndY=22.125 EndZ=0
    g9: LineSegment StartX=-11.4 StartY=22.125 StartZ=0 EndX=-11.4 EndY=15.75 EndZ=0
    g10: LineSegment StartX=-11.4 StartY=15.75 StartZ=0 EndX=-10.4 EndY=15.75 EndZ=0
    g11: LineSegment StartX=-10.4 StartY=15.75 StartZ=0 EndX=-10.4 EndY=14.25 EndZ=0
    g12: LineSegment StartX=-10.4 StartY=14.25 StartZ=0 EndX=-11.4 EndY=14.25 EndZ=0
    g13: LineSegment StartX=-11.4 StartY=14.25 StartZ=0 EndX=-11.4 EndY=7.875 EndZ=0
    g14: LineSegment StartX=-11.4 StartY=7.875 StartZ=0 EndX=-10.4 EndY=7.875 EndZ=0
    g15: LineSegment StartX=-10.4 StartY=7.875 StartZ=0 EndX=-10.4 EndY=6.375 EndZ=0
    g16: LineSegment StartX=-10.4 StartY=6.375 StartZ=0 EndX=-11.4 EndY=6.375 EndZ=0
    g17: LineSegment StartX=-11.4 StartY=6.375 StartZ=0 EndX=-11.4 EndY=0 EndZ=0
  constraints (53):
    c: PointOnObject(g4,g-1)
    c: Horizontal(g0)
    c: Coincident(g1,g2)
    c: Horizontal(g2)
    c: Coincident(g2,g3)
    c: Coincident(g3,g-1)
    c: Vertical(g3)
    c: Coincident(g3,g4)
    c: Distance(g4) = 11.4
    c: Distance(g2) = 6
    c: Distance(g3) = 50
    c: Coincident(g0,g1)
    c: Distance(g0,g3) = 12.5
    c: Coincident(g0,g5)
    c: Vertical(g5)
    c: Coincident(g5,g6)
    c: Horizontal(g6)
    c: Coincident(g6,g7)
    c: Coincident(g7,g8)
    c: Horizontal(g8)
    c: Coincident(g8,g9)
    c: Vertical(g9)
    c: Coincident(g9,g10)
    c: Horizontal(g10)
    c: Coincident(g10,g11)
    c: Coincident(g11,g12)
    c: Horizontal(g12)
    c: Coincident(g12,g13)
    c: Vertical(g13)
    c: Coincident(g13,g14)
    c: Coincident(g14,g15)
    c: Coincident(g15,g16)
    c: Horizontal(g16)
    c: Coincident(g16,g17)
    c: Vertical(g17)
    c: Coincident(g17,g4)
    c: Horizontal(g14)
    c: Vertical(g7)
    c: PointOnObject(g13,g17)
    c: PointOnObject(g8,g5)
    c: Equal(g12,g10)
    c: Equal(g10,g8)
    c: Equal(g6,g16)
    c: Equal(g16,g14)
    c: Equal(g11,g7)
    c: Equal(g7,g15)
    c: Distance(g12) = 1
    c: Distance(g15) = 1.5
    c: Equal(g9,g13)
    c: Equal(g5,g17)
    c: PointOnObject(g5,g17)
    c: Equal(g9,g5)
    c: DistanceY(g-1,g0) = 30
FEATURE [Part::Revolution] Revolve
  Angle = 360
  Axis = (0,0,1)
  Base = (0,0,0)
  FaceMakerClass = Part::FaceMakerBullseye
  Solid = true
  Source = -> Sketch032
  Symmetric = false
FEATURE [Sketcher::SketchObject] Sketch033
  ArcFitTolerance = 0
  AttachmentSupport = -> [Revolve]
  FullyConstrained = false
  MakeInternals = false
  MapMode = 5
  Placement = pos=(0,0,0) rot=(1,0,0;3.14159rad)
  sketch-geometry (1):
    g0: Circle CenterX=0 CenterY=0 CenterZ=0 NormalX=0 NormalY=0 NormalZ=1 AngleXU=0 Radius=2.43945
  constraints (1):
    c: Coincident(g0,g-1)
FEATURE [PartDesign::FeatureBase] BaseFeature
  BaseFeature = -> Revolve
  Suppressed = false
FEATURE [PartDesign::Hole] Hole
  BaseFeature = -> BaseFeature
  CustomThreadClearance = 0
  Depth = 140.626
  DepthType = 1
  Diameter = 6.828
  DrillForDepth = false
  DrillPoint = 1
  DrillPointAngle = 118
  HoleCutCountersinkAngle = 90
  HoleCutCustomValues = false
  HoleCutDepth = 0
  HoleCutDiameter = 6.1
  HoleCutType = 0
  ModelThread = true
  Profile = -> Sketch033
  Suppressed = false
  Tapered = false
  TaperedAngle = 90
  ThreadClass = 0
  ThreadDepth = 123.699
  ThreadDepthType = 0
  ThreadDirection = 0
  ThreadFit = 0
  ThreadSize = 16
  ThreadType = 1
  Threaded = true
  UseCustomThreadClearance = false
FEATURE [PartDesign::Body] Body008  label="truss_insert"
  AllowCompound = false
  BaseFeature = -> Revolve
  Group = -> [BaseFeature,Sketch033,Hole]
  Origin = -> Origin030
  Placement = pos=(-222.641,-73.8156,1104.16) rot=(0.983136,0.182135,0.016437;0.238199rad)
  Tip = -> Hole
FEATURE [Sketcher::SketchObject] Sketch034
  ArcFitTolerance = 0
  FullyConstrained = true
  MakeInternals = false
  Placement = pos=(0,0,0) rot=(1,0,0;1.5708rad)
  sketch-geometry (6):
    g0: LineSegment StartX=-11.5 StartY=0 StartZ=0 EndX=-11.5 EndY=30 EndZ=0
    g1: LineSegment StartX=-11.5 StartY=30 StartZ=0 EndX=-12.5 EndY=30 EndZ=0
    g2: LineSegment StartX=-12.5 StartY=30 StartZ=0 EndX=-6 EndY=50 EndZ=0
    g3: LineSegment StartX=-6 StartY=50 StartZ=0 EndX=0 EndY=50 EndZ=0
    g4: LineSegment StartX=0 StartY=50 StartZ=0 EndX=0 EndY=0 EndZ=0
    g5: LineSegment StartX=0 StartY=0 StartZ=0 EndX=-11.5 EndY=0 EndZ=0
  constraints (17):
    c: PointOnObject(g0,g-1)
    c: Vertical(g0)
    c: Coincident(g0,g1)
    c: Horizontal(g1)
    c: Coincident(g2,g3)
    c: Horizontal(g3)
    c: Coincident(g3,g4)
    c: Coincident(g4,g-1)
    c: Vertical(g4)
    c: Coincident(g4,g5)
    c: Coincident(g5,g0)
    c: Distance(g5) = 11.5
    c: Distance(g0) = 30
    c: Distance(g1) = 1
    c: Distance(g3) = 6
    c: Distance(g4) = 50
    c: Coincident(g1,g2)
FEATURE [Part::Revolution] Revolve001
  Angle = 360
  Axis = (0,0,1)
  Base = (0,0,0)
  FaceMakerClass = Part::FaceMakerBullseye
  Solid = true
  Source = -> Sketch034
  Symmetric = false
FEATURE [PartDesign::FeatureBase] BaseFeature001
  BaseFeature = -> Revolve001
  Suppressed = false
FEATURE [Sketcher::SketchObject] Sketch035
  ArcFitTolerance = 0
  AttachmentSupport = -> [Revolve001]
  FullyConstrained = false
  MakeInternals = false
  MapMode = 5
  Placement = pos=(0,0,50) rot=(0,0,1;0rad)
  sketch-geometry (1):
    g0: Circle CenterX=0 CenterY=0 CenterZ=0 NormalX=0 NormalY=0 NormalZ=1 AngleXU=0 Radius=2.43945
  constraints (1):
    c: Coincident(g0,g-1)
FEATURE [PartDesign::Hole] Hole001
  BaseFeature = -> BaseFeature001
  CustomThreadClearance = 0
  Depth = 140.626
  DepthType = 1
  Diameter = 6.828
  DrillForDepth = false
  DrillPoint = 1
  DrillPointAngle = 118
  HoleCutCountersinkAngle = 90
  HoleCutCustomValues = false
  HoleCutDepth = 0
  HoleCutDiameter = 6.1
  HoleCutType = 0
  ModelThread = true
  Profile = -> Sketch035
  Suppressed = false
  Tapered = false
  TaperedAngle = 90
  ThreadClass = 0
  ThreadDepth = 123.699
  ThreadDepthType = 0
  ThreadDirection = 0
  ThreadFit = 0
  ThreadSize = 16
  ThreadType = 1
  Threaded = true
  UseCustomThreadClearance = false
FEATURE [PartDesign::Body] Body009  label="truss_insert001"
  AllowCompound = false
  BaseFeature = -> Revolve001
  Group = -> [BaseFeature001,Sketch035,Hole001]
  Origin = -> Origin031
  Placement = pos=(-264.203,145.183,177.377) rot=(-0.011052,0.99246,0.122071;3.17398rad)
  Tip = -> Hole001
FEATURE [Sketcher::SketchObject] Sketch036  label="cf-mating-plate"
  ArcFitTolerance = 0
  FullyConstrained = true
  MakeInternals = false
  expr: Constraints[4] = <<secondary_stalk_sketch>>.Constraints[1]
  expr: Constraints[5] = Constraints[4] * sqrt(2)
  sketch-geometry (6):
    g0: Ellipse CenterX=0 CenterY=0 CenterZ=0 NormalX=0 NormalY=0 NormalZ=1 MajorRadius=45.9619 MinorRadius=32.5 AngleXU=-1.5708
    g1: LineSegment [constr] StartX=0 StartY=-45.9619 StartZ=0 EndX=0 EndY=45.9619 EndZ=0
    g2: LineSegment [constr] StartX=32.5 StartY=1.81594e-11 StartZ=0 EndX=-32.5 EndY=-1.81594e-11 EndZ=0
    g3: GeomPoint [constr] X=-1.81566e-11 Y=-32.5 Z=0
    g4: GeomPoint [constr] X=1.81594e-11 Y=32.5 Z=0
    g5: Circle CenterX=0 CenterY=0 CenterZ=0 NormalX=0 NormalY=0 NormalZ=1 AngleXU=0 Radius=1.5
  constraints (7):
    c: InternalAlignment(g1-g4 -> g0) x4
    c: Distance(g2) = 65
    c: Distance(g1) = 91.9239
    c: Coincident(g0,g-1)
    c: Coincident(g5,g0)
    c: Diameter(g5) = 3
    c: PointOnObject(g1,g-2)
FEATURE [Part::Extrusion] Extrude017  label="cf_mating-plate-extrude"
  Base = -> Sketch036
  Dir = (0,0,1)
  DirMode = 2
  FaceMakerClass = Part::FaceMakerBullseye
  FaceMakerMode = 3
  LengthFwd = 2
  LengthRev = 0
  Placement = pos=(-0.321426,1.23535,85.4596) rot=(0.899618,0.178243,0.398644;0.864663rad)
  Solid = true
  Symmetric = false
FEATURE [App::Part] Part003  label="spider"
  Group = -> [Array013,Sketch005,Extrude013,Extrude012,Sketch028,Cut,Sketch027,Slice,Extrude011,Sketch029,Extrude014,Slice_child0,Sketch030,Extrude015,Sketch036,Extrude017]
  Origin = -> Origin021
FEATURE [Sketcher::SketchObject] Sketch037  label="lower_uta_bracket_sketch"
  ArcFitTolerance = 0
  FullyConstrained = true
  MakeInternals = false
  MapMode = 5
  expr: Constraints[13] = Constraints[12]
  expr: Constraints[1] = <<uta_ring>>.Constraints[1]
  expr: Constraints[3] = <<uta_ring>>.Constraints[3]
  expr: Constraints[4] = <<mounting_hole>>.Constraints[1]
  expr: Constraints[52] = Constraints[8] - 6 mm
  expr: Constraints[53] = Constraints[8] + 6 mm
  expr: Constraints[8] = <<mounting_hole>>.Constraints[0]
  sketch-geometry (30):
    g0: ArcOfCircle CenterX=-2e-16 CenterY=1.7e-15 CenterZ=0 NormalX=0 NormalY=0 NormalZ=1 AngleXU=0 Radius=225 StartAngle=1.45386 EndAngle=1.68773
    g1: ArcOfCircle CenterX=-2e-16 CenterY=1.7e-15 CenterZ=0 NormalX=0 NormalY=0 NormalZ=1 AngleXU=0 Radius=255 StartAngle=1.45386 EndAngle=1.68773
    g2: Circle CenterX=0 CenterY=240 CenterZ=0 NormalX=0 NormalY=0 NormalZ=1 AngleXU=0 Radius=3
    g3: LineSegment StartX=-29.751 StartY=253.259 StartZ=0 EndX=-28.351 EndY=241.34 EndZ=0
    g4: LineSegment StartX=29.751 StartY=253.259 StartZ=0 EndX=28.351 EndY=241.34 EndZ=0
    g5: LineSegment [constr] StartX=29.751 StartY=253.259 StartZ=0 EndX=-2e-16 EndY=1.7e-15 EndZ=0
    g6: LineSegment [constr] StartX=-29.751 StartY=253.259 StartZ=0 EndX=7e-16 EndY=1.5e-15 EndZ=0
    g7: ArcOfCircle [constr] CenterX=-2e-16 CenterY=1.7e-15 CenterZ=0 NormalX=0 NormalY=0 NormalZ=1 AngleXU=0 Radius=240 StartAngle=1.45386 EndAngle=1.68773
    g8: LineSegment [constr] StartX=0 StartY=255 StartZ=0 EndX=-2e-16 EndY=0 EndZ=0
    g9: ArcOfCircle CenterX=-15.9911 CenterY=239.467 CenterZ=0 NormalX=0 NormalY=0 NormalZ=1 AngleXU=0 Radius=7.5 StartAngle=3.63415 EndAngle=9.09422
    g10: ArcOfCircle CenterX=15.9911 CenterY=239.467 CenterZ=0 NormalX=0 NormalY=0 NormalZ=1 AngleXU=0 Radius=7.5 StartAngle=0.330561 EndAngle=5.79062
    g11: Circle [constr] CenterX=-15.9911 CenterY=239.467 CenterZ=0 NormalX=0 NormalY=0 NormalZ=1 AngleXU=0 Radius=10
    g12: Circle [constr] CenterX=15.9911 CenterY=239.467 CenterZ=0 NormalX=0 NormalY=0 NormalZ=1 AngleXU=0 Radius=10
    g13: Circle [constr] CenterX=0 CenterY=240 CenterZ=0 NormalX=0 NormalY=0 NormalZ=1 AngleXU=0 Radius=6
    g14: Circle [constr] CenterX=-25.375 CenterY=249.775 CenterZ=0 NormalX=0 NormalY=0 NormalZ=1 AngleXU=0 Radius=3.93965
    g15: Circle CenterX=-25.375 CenterY=249.775 CenterZ=0 NormalX=0 NormalY=0 NormalZ=1 AngleXU=0 Radius=1.5
    g16: Circle [constr] CenterX=25.375 CenterY=249.775 CenterZ=0 NormalX=0 NormalY=0 NormalZ=1 AngleXU=0 Radius=3.93965
    g17: Circle [constr] CenterX=22.9544 CenterY=227.602 CenterZ=0 NormalX=0 NormalY=0 NormalZ=1 AngleXU=0 Radius=3.75687
    g18: Circle [constr] CenterX=-22.9544 CenterY=227.602 CenterZ=0 NormalX=0 NormalY=0 NormalZ=1 AngleXU=0 Radius=3.75687
    g19: Circle CenterX=25.375 CenterY=249.775 CenterZ=0 NormalX=0 NormalY=0 NormalZ=1 AngleXU=0 Radius=1.5
    g20: Circle CenterX=22.9544 CenterY=227.602 CenterZ=0 NormalX=0 NormalY=0 NormalZ=1 AngleXU=0 Radius=1.5
    g21: Circle CenterX=-22.9544 CenterY=227.602 CenterZ=0 NormalX=0 NormalY=0 NormalZ=1 AngleXU=0 Radius=1.5
    g22: ArcOfCircle [constr] CenterX=-2e-16 CenterY=1.7e-15 CenterZ=0 NormalX=0 NormalY=0 NormalZ=1 AngleXU=0 Radius=243 StartAngle=1.45386 EndAngle=1.68773
    g23: ArcOfCircle [constr] CenterX=-2e-16 CenterY=1.7e-15 CenterZ=0 NormalX=0 NormalY=0 NormalZ=1 AngleXU=0 Radius=237 StartAngle=1.45386 EndAngle=1.68773
    g24: ArcOfCircle CenterX=1.297e-12 CenterY=1.708e-13 CenterZ=0 NormalX=0 NormalY=0 NormalZ=1 AngleXU=0 Radius=237 StartAngle=1.6663 EndAngle=1.68773
    g25: ArcOfCircle CenterX=1.2797e-12 CenterY=-1.418e-13 CenterZ=0 NormalX=0 NormalY=0 NormalZ=1 AngleXU=0 Radius=237 StartAngle=1.45386 EndAngle=1.47529
    g26: ArcOfCircle CenterX=-1.2186e-12 CenterY=1.245e-13 CenterZ=0 NormalX=0 NormalY=0 NormalZ=1 AngleXU=0 Radius=243 StartAngle=1.45386 EndAngle=1.47565
    g27: LineSegment StartX=27.651 StartY=235.381 StartZ=0 EndX=26.2509 EndY=223.463 EndZ=0
    g28: LineSegment StartX=-27.651 StartY=235.381 StartZ=0 EndX=-26.2509 EndY=223.463 EndZ=0
    g29: ArcOfCircle CenterX=-2e-16 CenterY=1.7e-15 CenterZ=0 NormalX=0 NormalY=0 NormalZ=1 AngleXU=0 Radius=243 StartAngle=1.66594 EndAngle=1.68773
  constraints (88):
    c: Coincident(g0,g-1)
    c: Diameter(g0) = 450
    c: Coincident(g1,g0)
    c: Diameter(g1) = 510
    c: Diameter(g2) = 6
    c: Coincident(g5,g0)
    c: Coincident(g6,g0)
    c: Coincident(g7,g0)
    c: Diameter(g7) = 480
    c: PointOnObject(g2,g7)
    c: Coincident(g8,g0)
    c: PointOnObject(g2,g8)
    c: Angle(g8,g6) = 0.116937
    c: Angle(g5,g8) = 0.116937
    c: PointOnObject(g9,g7)
    c: Equal(g9,g10)
    c: Diameter(g9) = 15
    c: Symmetric(g9,g10,g8)
    c: Coincident(g11,g9)
    c: Coincident(g12,g10)
    c: Equal(g12,g11)
    c: Diameter(g11) = 20
    c: Coincident(g13,g2)
    c: Diameter(g13) = 12
    c: PointOnObject(g2,g-2)
    c: PointOnObject(g4,g5)
    c: PointOnObject(g28,g6)
    c: PointOnObject(g3,g6)
    c: PointOnObject(g5,g1)
    c: PointOnObject(g6,g1)
    c: PointOnObject(g8,g1)
    c: Tangent(g11,g13)
    c: Tangent(g14,g11)
    c: Tangent(g14,g1)
    c: Coincident(g15,g14)
    c: Diameter(g15) = 3
    c: Tangent(g18,g11)
    c: Tangent(g17,g12)
    c: Tangent(g16,g1)
    c: Tangent(g16,g12)
    c: Coincident(g19,g16)
    c: Coincident(g20,g17)
    c: Coincident(g21,g18)
    c: Equal(g19,g20)
    c: Equal(g20,g21)
    c: Equal(g21,g15)
    c: Coincident(g22,g0)
    c: PointOnObject(g22,g6)
    c: PointOnObject(g22,g5)
    c: Coincident(g23,g0)
    c: PointOnObject(g23,g6)
    c: PointOnObject(g23,g5)
    c: Diameter(g23) = 474
    c: Diameter(g22) = 486
    c: PointOnObject(g24,g9)
    c: PointOnObject(g24,g23)
    c: Equal(g24,g23)
    c: Equal(g25,g23)
    c: PointOnObject(g25,g23)
    c: PointOnObject(g26,g10)
    c: PointOnObject(g26,g22)
    c: Equal(g26,g22)
    c: PointOnObject(g9,g23)
    c: Coincident(g10,g25)
    c: PointOnObject(g10,g22)
    c: Coincident(g3,g22)
    c: Coincident(g25,g27)
    c: Coincident(g25,g23)
    c: Coincident(g26,g22)
    c: Coincident(g26,g4)
    c: Coincident(g0,g28)
    c: Coincident(g1,g4)
    c: Coincident(g3,g1)
    c: Coincident(g0,g27)
    c: PointOnObject(g7,g5)
    c: PointOnObject(g7,g6)
    c: PointOnObject(g0,g5)
    c: Tangent(g18,g0)
    c: Tangent(g18,g28)
    c: Tangent(g17,g0)
    c: Tangent(g17,g27)
    c: Tangent(g16,g4)
    c: Tangent(g14,g3)
    c: Coincident(g28,g24)
    c: Coincident(g23,g24)
    c: Coincident(g29,g0)
    c: Coincident(g29,g3)
    c: Coincident(g29,g9)
FEATURE [Part::Extrusion] Extrude018  label="lower_bracket_extrude"
  Base = -> Sketch037
  Dir = (0,0,1)
  DirMode = 2
  FaceMakerClass = Part::FaceMakerBullseye
  FaceMakerMode = 3
  LengthFwd = 4.8
  LengthRev = 0
  Solid = true
  Symmetric = false
FEATURE [Part::Fillet] Fillet
  Base = -> Extrude018
  EdgeLinks = -> Extrude018 [Edge2,Edge5,Edge20,Edge23]
  Edges = 4 edges r=3: [Edge2,Edge5,Edge20,Edge23]
FEATURE [Part::Fillet] Fillet001  label="lower_bracket_fillet"
  Base = -> Fillet
  EdgeLinks = -> Fillet [Edge2,Edge28,Edge48,Edge50,Edge51,Edge53,Edge55,Edge57]
  Edges = 8 edges r=1: [Edge2,Edge28,Edge48,Edge50,Edge51,Edge53,Edge55,Edge57]
  Placement = pos=(0,0,-18) rot=(0,0,1;0rad)
FEATURE [Part::Fillet] Fillet002  label="upper_bracket_fillet"
  Base = -> Extrude010
  EdgeLinks = -> Extrude010 [Edge1,Edge2,Edge5,Edge8]
  Edges = 4 edges r=3: [Edge1,Edge2,Edge5,Edge8]
FEATURE [App::Part] Part004  label="upper_truss_mount"
  Group = -> [Sketch023,Extrude010,Sphere,Array011,Extrude018,Fillet,Fillet001,Fillet002]
  Origin = -> Origin022
  Placement = pos=(0,0,-4.8) rot=(0,0,1;-0.523599rad)
FEATURE [Part::FeaturePython] Array015  label="upper_truss_mounts"  # Draft array (typed FeaturePython)
  AlwaysSyncPlacement = false
  Angle = 360
  ArrayType = 1
  Axis = (0,0,1)
  Base = -> Part004
  Center = (0,0,0)
  Count = 3
  ExpandArray = false
  Fuse = false
  IntervalAxis = (0,0,0)
  IntervalX = (50,0,0)
  IntervalY = (0,50,0)
  IntervalZ = (0,0,50)
  NumberCircles = 3
  NumberPolar = 3
  NumberX = 2
  NumberY = 2
  NumberZ = 1
  PlacementList = 3 placements: [(0,0,-4.8),(0,0,-4.8),(0,0,-4.8)]
  RadialDistance = 50
  ScaleList = (3) [(1,1,1),(1,1,1),(1,1,1)]
  Symmetry = 1
  TangentialDistance = 25
FEATURE [App::Part] Part  label="uta"
  Group = -> [Part001,Part003,_2935K17_Nylon_Ribbed_Knob,Array007,Part004,Array015,Body,Array016,Part005]
  Origin = -> Origin018
  Placement = pos=(0,0,1232) rot=(0,0,1;-1.5708rad)
